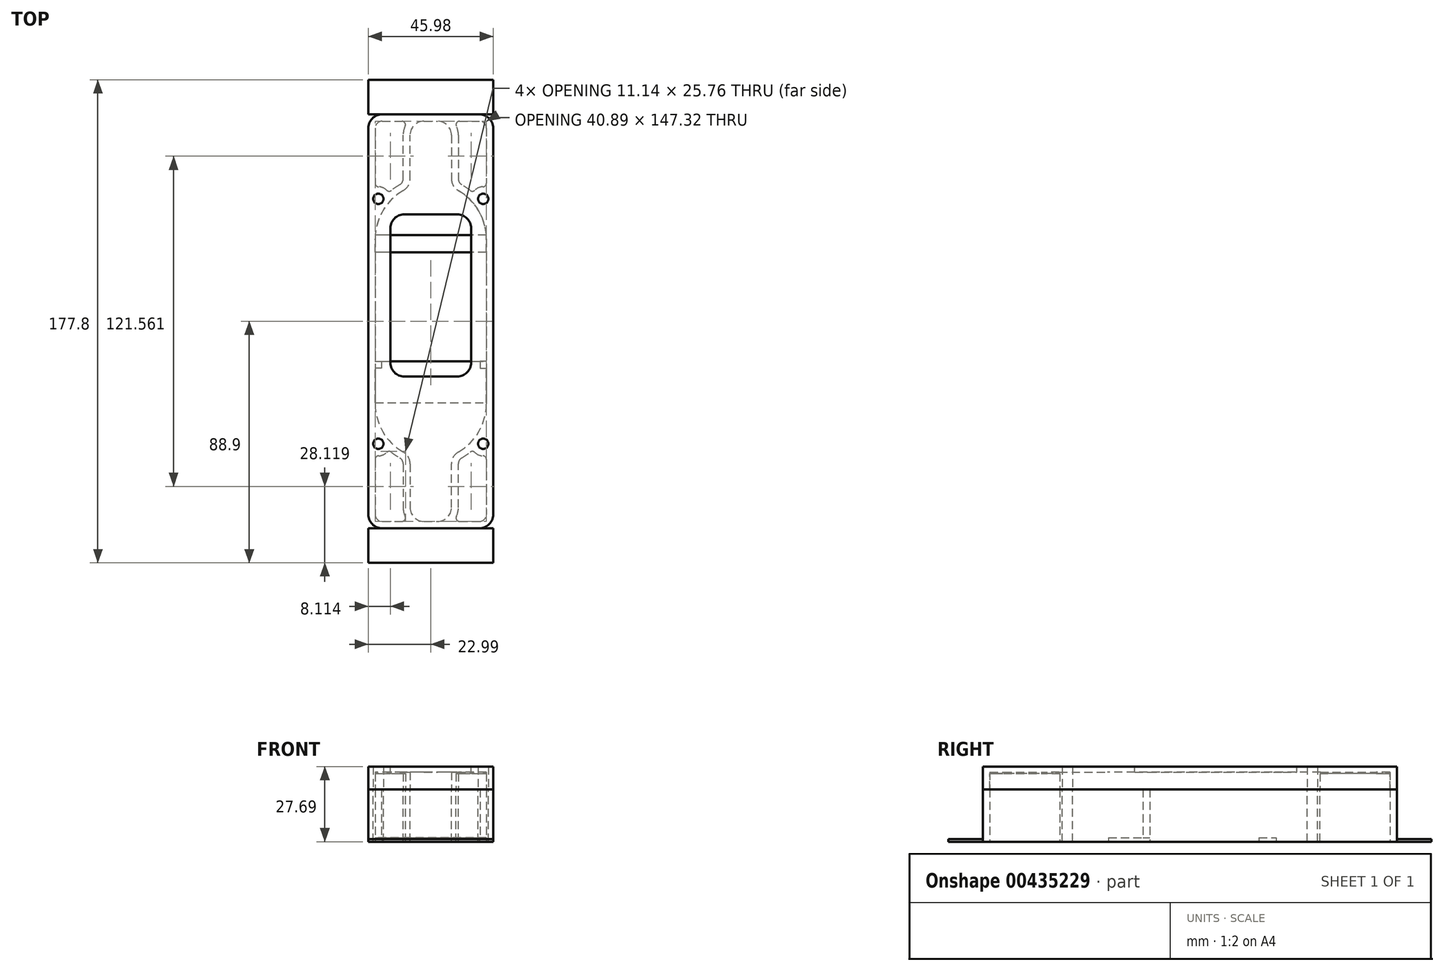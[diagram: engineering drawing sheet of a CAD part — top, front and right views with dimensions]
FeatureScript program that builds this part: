
annotation { "Feature Type Name" : "Feature", "Feature Type Description" : "" }
export const myFeature = defineFeature(function(context is Context, id is Id, definition is map)
    precondition{}
    {
        {
            var Q0;
            Q0=qCreatedBy(makeId("Top.planeOp"),FACE);
            var sketch = newSketch(context, id + "F0", { "sketchPlane" : qUnion([Q0])});
            skArc(sketch, "E0", {"start": v(20.45, 30.35) * mm, "mid": v(16.94, 41.8) * mm, "end": v(7.62, 49.33) * mm});
            skArc(sketch, "E1", {"start": v(-20.45, -30.35) * mm, "mid": v(-16.94, -41.8) * mm, "end": v(-7.62, -49.33) * mm});
            skLineSegment(sketch, "E2", {"start": v(20.45, 30.35) * mm, "end": v(20.45, -14.73) * mm});
            skLineSegment(sketch, "E3", {"start": v(-20.45, 30.35) * mm, "end": v(-20.45, -14.73) * mm});
            skPoint(sketch, "E4", {"position": v(0, 50.8) * mm});
            skPoint(sketch, "E5", {"position": v(0, -50.8) * mm});
            skPoint(sketch, "E6", {"position": v(-20.45, 0) * mm});
            skLineSegment(sketch, "E7", {"start": v(-20.45, -14.73) * mm, "end": v(-18.16, -14.73) * mm});
            skLineSegment(sketch, "E8", {"start": v(-18.16, -14.73) * mm, "end": v(-18.16, -17.27) * mm});
            skLineSegment(sketch, "E9", {"start": v(-18.16, -17.27) * mm, "end": v(-20.45, -17.27) * mm});
            skLineSegment(sketch, "E10", {"start": v(20.45, -14.73) * mm, "end": v(18.16, -14.73) * mm});
            skLineSegment(sketch, "E11", {"start": v(18.16, -14.73) * mm, "end": v(18.16, -17.27) * mm});
            skLineSegment(sketch, "E12", {"start": v(18.16, -17.27) * mm, "end": v(20.45, -17.27) * mm});
            skLineSegment(sketch, "E13", {"start": v(-20.45, -14.73) * mm, "end": v(-20.45, -17.27) * mm, "construction": true});
            skLineSegment(sketch, "E14", {"start": v(-20.45, -17.27) * mm, "end": v(-20.45, -30.35) * mm});
            skLineSegment(sketch, "E15", {"start": v(20.45, -17.27) * mm, "end": v(20.45, -30.35) * mm});
            skLineSegment(sketch, "E16", {"start": v(20.45, -14.73) * mm, "end": v(20.45, -17.27) * mm, "construction": true});
            skLineSegment(sketch, "E17", {"start": v(-18.16, -14.73) * mm, "end": v(18.16, -14.73) * mm, "construction": true});
            skPoint(sketch, "E18", {"position": v(0, -14.73) * mm});
            skLineSegment(sketch, "E19.bottom", {"start": v(-22.99, 76.2) * mm, "end": v(22.99, 76.2) * mm});
            skLineSegment(sketch, "E19.top", {"start": v(-22.99, -76.2) * mm, "end": v(22.99, -76.2) * mm});
            skLineSegment(sketch, "E19.left", {"start": v(-22.99, 76.2) * mm, "end": v(-22.99, -76.2) * mm});
            skLineSegment(sketch, "E19.right", {"start": v(22.99, 76.2) * mm, "end": v(22.99, -76.2) * mm});
            skPoint(sketch, "E20", {"position": v(0, 76.2) * mm});
            skPoint(sketch, "E21", {"position": v(-22.99, 0) * mm});
            skLineSegment(sketch, "E22", {"start": v(-7.62, 49.33) * mm, "end": v(-7.62, 73.66) * mm});
            skLineSegment(sketch, "E23", {"start": v(-7.62, 73.66) * mm, "end": v(7.62, 73.66) * mm});
            skLineSegment(sketch, "E24", {"start": v(7.62, 73.66) * mm, "end": v(7.62, 49.33) * mm});
            skArc(sketch, "E25", {"start": v(-7.62, 49.33) * mm, "mid": v(-16.94, 41.8) * mm, "end": v(-20.45, 30.35) * mm});
            skArc(sketch, "E26", {"start": v(7.62, 49.33) * mm, "mid": v(0, 50.8) * mm, "end": v(-7.62, 49.33) * mm, "construction": true});
            skLineSegment(sketch, "E27", {"start": v(-20.45, 30.35) * mm, "end": v(-22.99, 30.35) * mm, "construction": true});
            skLineSegment(sketch, "E28", {"start": v(-7.62, 73.66) * mm, "end": v(-7.62, 76.2) * mm, "construction": true});
            skLineSegment(sketch, "E29", {"start": v(-7.62, -49.33) * mm, "end": v(-7.62, -73.66) * mm});
            skLineSegment(sketch, "E30", {"start": v(-7.62, -73.66) * mm, "end": v(7.62, -73.66) * mm});
            skLineSegment(sketch, "E31", {"start": v(7.62, -73.66) * mm, "end": v(7.62, -49.33) * mm});
            skArc(sketch, "E32", {"start": v(7.62, -49.33) * mm, "mid": v(16.94, -41.8) * mm, "end": v(20.45, -30.35) * mm});
            skArc(sketch, "E33", {"start": v(-7.62, -49.33) * mm, "mid": v(0, -50.8) * mm, "end": v(7.62, -49.33) * mm, "construction": true});
            skSolve(sketch);
        }
        {
            var Q0;
            Q0 = qSketchRegion(id + "F0", true);
            extrude(context, id + "F1", {"entities" : qUnion([Q0]), "depth" : 19.3 * mm});
        }
        {
            var Q0;
            Q0=makeQuery(id+"F1.opExtrude","CAP_FACE",FACE,{"disambiguationData":[OSD([sQuery(id+"F0.wireOp",EDGE,"E0"),sQuery(id+"F0.wireOp",EDGE,"E1"),sQuery(id+"F0.wireOp",EDGE,"E2"),sQuery(id+"F0.wireOp",EDGE,"E3"),sQuery(id+"F0.wireOp",EDGE,"E7"),sQuery(id+"F0.wireOp",EDGE,"E8"),sQuery(id+"F0.wireOp",EDGE,"E9"),sQuery(id+"F0.wireOp",EDGE,"E10"),sQuery(id+"F0.wireOp",EDGE,"E11"),sQuery(id+"F0.wireOp",EDGE,"E12"),sQuery(id+"F0.wireOp",EDGE,"E14"),sQuery(id+"F0.wireOp",EDGE,"E15"),sQuery(id+"F0.wireOp",EDGE,"E19.bottom"),sQuery(id+"F0.wireOp",EDGE,"E19.top"),sQuery(id+"F0.wireOp",EDGE,"E19.left"),sQuery(id+"F0.wireOp",EDGE,"E19.right"),sQuery(id+"F0.wireOp",EDGE,"E22"),sQuery(id+"F0.wireOp",EDGE,"E23"),sQuery(id+"F0.wireOp",EDGE,"E24"),sQuery(id+"F0.wireOp",EDGE,"E25"),sQuery(id+"F0.wireOp",EDGE,"E29"),sQuery(id+"F0.wireOp",EDGE,"E30"),sQuery(id+"F0.wireOp",EDGE,"E31"),sQuery(id+"F0.wireOp",EDGE,"E32")])],"isStart":true});
            var sketch = newSketch(context, id + "F2", { "sketchPlane" : qUnion([Q0])});
            skLineSegment(sketch, "E34.bottom", {"start": v(-20.45, 29.97) * mm, "end": v(20.45, 29.97) * mm});
            skLineSegment(sketch, "E34.top", {"start": v(-20.45, 14.73) * mm, "end": v(20.45, 14.73) * mm});
            skLineSegment(sketch, "E34.left", {"start": v(-20.45, 29.97) * mm, "end": v(-20.45, 14.73) * mm});
            skLineSegment(sketch, "E34.right", {"start": v(20.45, 29.97) * mm, "end": v(20.45, 14.73) * mm});
            skLineSegment(sketch, "E35.bottom", {"start": v(20.45, -25.4) * mm, "end": v(-20.45, -25.4) * mm});
            skLineSegment(sketch, "E35.top", {"start": v(20.45, -31.75) * mm, "end": v(-20.45, -31.75) * mm});
            skLineSegment(sketch, "E35.left", {"start": v(20.45, -25.4) * mm, "end": v(20.45, -31.75) * mm});
            skLineSegment(sketch, "E35.right", {"start": v(-20.45, -25.4) * mm, "end": v(-20.45, -31.75) * mm});
            skPoint(sketch, "E36", {"position": v(-20.45, 22.35) * mm});
            skSolve(sketch);
        }
        {
            var Q0;
            Q0 = qSketchRegion(id + "F2", true);
            extrude(context, id + "F3", {"entities" : qUnion([Q0]), "operationType" : NewBodyOperationType.ADD, "oppositeDirection" : true, "depth" : 1.52 * mm});
        }
        {
            var Q0;
            Q0=makeQuery(id+"FgRfp3muFPT9lto_1.boolean.opBoolean","MERGE",EDGE,{"derivedFrom":[makeQuery(id+"F1.opExtrude","SWEPT_EDGE",EDGE,{"disambiguationData":[OSD([sQuery(id+"F0.wireOp",EDGE,"E19.bottom"),sQuery(id+"F0.wireOp",EDGE,"E19.left")])]}),makeQuery(id+"FgRfp3muFPT9lto_1.opExtrude","SWEPT_EDGE",EDGE,{"disambiguationData":[OSD([sQuery(id+"Ftx3Hq8NVKijBld_1.wireOp",EDGE,"g6n0YkWi-r8fi-JQox-6JIj-wQ41cYzrdf4m.top"),sQuery(id+"Ftx3Hq8NVKijBld_1.wireOp",EDGE,"g6n0YkWi-r8fi-JQox-6JIj-wQ41cYzrdf4m.right")])]})]});
            var Q1;
            Q1=makeQuery(id+"FgRfp3muFPT9lto_1.boolean.opBoolean","MERGE",EDGE,{"derivedFrom":[makeQuery(id+"F1.opExtrude","SWEPT_EDGE",EDGE,{"disambiguationData":[OSD([sQuery(id+"F0.wireOp",EDGE,"E19.top"),sQuery(id+"F0.wireOp",EDGE,"E19.left")])]}),makeQuery(id+"FgRfp3muFPT9lto_1.opExtrude","SWEPT_EDGE",EDGE,{"disambiguationData":[OSD([sQuery(id+"Ftx3Hq8NVKijBld_1.wireOp",EDGE,"g6n0YkWi-r8fi-JQox-6JIj-wQ41cYzrdf4m.bottom"),sQuery(id+"Ftx3Hq8NVKijBld_1.wireOp",EDGE,"g6n0YkWi-r8fi-JQox-6JIj-wQ41cYzrdf4m.right")])]})]});
            var Q2;
            Q2=makeQuery(id+"FgRfp3muFPT9lto_1.boolean.opBoolean","MERGE",EDGE,{"derivedFrom":[makeQuery(id+"F1.opExtrude","SWEPT_EDGE",EDGE,{"disambiguationData":[OSD([sQuery(id+"F0.wireOp",EDGE,"E19.top"),sQuery(id+"F0.wireOp",EDGE,"E19.right")])]}),makeQuery(id+"FgRfp3muFPT9lto_1.opExtrude","SWEPT_EDGE",EDGE,{"disambiguationData":[OSD([sQuery(id+"Ftx3Hq8NVKijBld_1.wireOp",EDGE,"g6n0YkWi-r8fi-JQox-6JIj-wQ41cYzrdf4m.bottom"),sQuery(id+"Ftx3Hq8NVKijBld_1.wireOp",EDGE,"g6n0YkWi-r8fi-JQox-6JIj-wQ41cYzrdf4m.left")])]})]});
            var Q3;
            Q3=makeQuery(id+"FgRfp3muFPT9lto_1.boolean.opBoolean","MERGE",EDGE,{"derivedFrom":[makeQuery(id+"F1.opExtrude","SWEPT_EDGE",EDGE,{"disambiguationData":[OSD([sQuery(id+"F0.wireOp",EDGE,"E19.bottom"),sQuery(id+"F0.wireOp",EDGE,"E19.right")])]}),makeQuery(id+"FgRfp3muFPT9lto_1.opExtrude","SWEPT_EDGE",EDGE,{"disambiguationData":[OSD([sQuery(id+"Ftx3Hq8NVKijBld_1.wireOp",EDGE,"g6n0YkWi-r8fi-JQox-6JIj-wQ41cYzrdf4m.top"),sQuery(id+"Ftx3Hq8NVKijBld_1.wireOp",EDGE,"g6n0YkWi-r8fi-JQox-6JIj-wQ41cYzrdf4m.left")])]})]});
            var Q4;
            Q4=makeQuery(id+"FgRfp3muFPT9lto_1.boolean.opBoolean","MERGE",EDGE,{"derivedFrom":[makeQuery(id+"F1.opExtrude","SWEPT_EDGE",EDGE,{"disambiguationData":[OSD([sQuery(id+"F0.wireOp",EDGE,"E23"),sQuery(id+"F0.wireOp",EDGE,"E24")])]}),makeQuery(id+"FgRfp3muFPT9lto_1.opExtrude","SWEPT_EDGE",EDGE,{"disambiguationData":[OSD([sQuery(id+"Ftx3Hq8NVKijBld_1.wireOp",EDGE,"3AGzFTSj-HEBm-45NR-ugF2-llzYKDWyuuH7.bottom"),sQuery(id+"Ftx3Hq8NVKijBld_1.wireOp",EDGE,"3AGzFTSj-HEBm-45NR-ugF2-llzYKDWyuuH7.left")])]})]});
            var Q5;
            Q5=makeQuery(id+"FgRfp3muFPT9lto_1.boolean.opBoolean","MERGE",EDGE,{"derivedFrom":[makeQuery(id+"F1.opExtrude","SWEPT_EDGE",EDGE,{"disambiguationData":[OSD([sQuery(id+"F0.wireOp",EDGE,"E22"),sQuery(id+"F0.wireOp",EDGE,"E23")])]}),makeQuery(id+"FgRfp3muFPT9lto_1.opExtrude","SWEPT_EDGE",EDGE,{"disambiguationData":[OSD([sQuery(id+"Ftx3Hq8NVKijBld_1.wireOp",EDGE,"3AGzFTSj-HEBm-45NR-ugF2-llzYKDWyuuH7.bottom"),sQuery(id+"Ftx3Hq8NVKijBld_1.wireOp",EDGE,"3AGzFTSj-HEBm-45NR-ugF2-llzYKDWyuuH7.right")])]})]});
            var Q6;
            Q6=makeQuery(id+"F1.opExtrude","SWEPT_EDGE",EDGE,{"disambiguationData":[OSD([sQuery(id+"F0.wireOp",EDGE,"E22"),sQuery(id+"F0.wireOp",EDGE,"E25")])]});
            var Q7;
            Q7=makeQuery(id+"F1.opExtrude","SWEPT_EDGE",EDGE,{"disambiguationData":[OSD([sQuery(id+"F0.wireOp",EDGE,"E0"),sQuery(id+"F0.wireOp",EDGE,"E24")])]});
            var Q8;
            Q8=makeQuery(id+"F1.opExtrude","SWEPT_EDGE",EDGE,{"disambiguationData":[OSD([sQuery(id+"F0.wireOp",EDGE,"E1"),sQuery(id+"F0.wireOp",EDGE,"E29")])]});
            var Q9;
            Q9=makeQuery(id+"FgRfp3muFPT9lto_1.boolean.opBoolean","MERGE",EDGE,{"derivedFrom":[makeQuery(id+"F1.opExtrude","SWEPT_EDGE",EDGE,{"disambiguationData":[OSD([sQuery(id+"F0.wireOp",EDGE,"E29"),sQuery(id+"F0.wireOp",EDGE,"E30")])]}),makeQuery(id+"FgRfp3muFPT9lto_1.opExtrude","SWEPT_EDGE",EDGE,{"disambiguationData":[OSD([sQuery(id+"Ftx3Hq8NVKijBld_1.wireOp",EDGE,"SY61azI3-jvyg-wfIl-SQMA-vttAN6HS4ba1.bottom"),sQuery(id+"Ftx3Hq8NVKijBld_1.wireOp",EDGE,"SY61azI3-jvyg-wfIl-SQMA-vttAN6HS4ba1.right")])]})]});
            var Q10;
            Q10=makeQuery(id+"FgRfp3muFPT9lto_1.boolean.opBoolean","MERGE",EDGE,{"derivedFrom":[makeQuery(id+"F1.opExtrude","SWEPT_EDGE",EDGE,{"disambiguationData":[OSD([sQuery(id+"F0.wireOp",EDGE,"E30"),sQuery(id+"F0.wireOp",EDGE,"E31")])]}),makeQuery(id+"FgRfp3muFPT9lto_1.opExtrude","SWEPT_EDGE",EDGE,{"disambiguationData":[OSD([sQuery(id+"Ftx3Hq8NVKijBld_1.wireOp",EDGE,"SY61azI3-jvyg-wfIl-SQMA-vttAN6HS4ba1.bottom"),sQuery(id+"Ftx3Hq8NVKijBld_1.wireOp",EDGE,"SY61azI3-jvyg-wfIl-SQMA-vttAN6HS4ba1.left")])]})]});
            var Q11;
            Q11=makeQuery(id+"F1.opExtrude","SWEPT_EDGE",EDGE,{"disambiguationData":[OSD([sQuery(id+"F0.wireOp",EDGE,"E31"),sQuery(id+"F0.wireOp",EDGE,"E32")])]});
            var Q12;
            Q12=makeQuery(id+"FgRfp3muFPT9lto_1.opExtrude","SWEPT_EDGE",EDGE,{"disambiguationData":[OSD([sQuery(id+"Ftx3Hq8NVKijBld_1.wireOp",EDGE,"3AGzFTSj-HEBm-45NR-ugF2-llzYKDWyuuH7.top"),sQuery(id+"Ftx3Hq8NVKijBld_1.wireOp",EDGE,"3AGzFTSj-HEBm-45NR-ugF2-llzYKDWyuuH7.right")])]});
            var Q13;
            Q13=makeQuery(id+"FgRfp3muFPT9lto_1.opExtrude","SWEPT_EDGE",EDGE,{"disambiguationData":[OSD([sQuery(id+"Ftx3Hq8NVKijBld_1.wireOp",EDGE,"3AGzFTSj-HEBm-45NR-ugF2-llzYKDWyuuH7.top"),sQuery(id+"Ftx3Hq8NVKijBld_1.wireOp",EDGE,"3AGzFTSj-HEBm-45NR-ugF2-llzYKDWyuuH7.left")])]});
            var Q14;
            Q14=makeQuery(id+"FgRfp3muFPT9lto_1.opExtrude","SWEPT_EDGE",EDGE,{"disambiguationData":[OSD([sQuery(id+"Ftx3Hq8NVKijBld_1.wireOp",EDGE,"f7xWbKYU-4XlC-xXvP-zV3z-Gg6iEQBUtCaq.bottom"),sQuery(id+"Ftx3Hq8NVKijBld_1.wireOp",EDGE,"f7xWbKYU-4XlC-xXvP-zV3z-Gg6iEQBUtCaq.right")])]});
            var Q15;
            Q15=makeQuery(id+"FgRfp3muFPT9lto_1.opExtrude","SWEPT_EDGE",EDGE,{"disambiguationData":[OSD([sQuery(id+"Ftx3Hq8NVKijBld_1.wireOp",EDGE,"f7xWbKYU-4XlC-xXvP-zV3z-Gg6iEQBUtCaq.bottom"),sQuery(id+"Ftx3Hq8NVKijBld_1.wireOp",EDGE,"f7xWbKYU-4XlC-xXvP-zV3z-Gg6iEQBUtCaq.left")])]});
            var Q16;
            Q16=makeQuery(id+"FgRfp3muFPT9lto_1.opExtrude","SWEPT_EDGE",EDGE,{"disambiguationData":[OSD([sQuery(id+"Ftx3Hq8NVKijBld_1.wireOp",EDGE,"SY61azI3-jvyg-wfIl-SQMA-vttAN6HS4ba1.top"),sQuery(id+"Ftx3Hq8NVKijBld_1.wireOp",EDGE,"SY61azI3-jvyg-wfIl-SQMA-vttAN6HS4ba1.right")])]});
            var Q17;
            Q17=makeQuery(id+"FgRfp3muFPT9lto_1.opExtrude","SWEPT_EDGE",EDGE,{"disambiguationData":[OSD([sQuery(id+"Ftx3Hq8NVKijBld_1.wireOp",EDGE,"SY61azI3-jvyg-wfIl-SQMA-vttAN6HS4ba1.top"),sQuery(id+"Ftx3Hq8NVKijBld_1.wireOp",EDGE,"SY61azI3-jvyg-wfIl-SQMA-vttAN6HS4ba1.left")])]});
            var Q18;
            Q18=makeQuery(id+"FgRfp3muFPT9lto_1.opExtrude","SWEPT_EDGE",EDGE,{"disambiguationData":[OSD([sQuery(id+"Ftx3Hq8NVKijBld_1.wireOp",EDGE,"f7xWbKYU-4XlC-xXvP-zV3z-Gg6iEQBUtCaq.top"),sQuery(id+"Ftx3Hq8NVKijBld_1.wireOp",EDGE,"f7xWbKYU-4XlC-xXvP-zV3z-Gg6iEQBUtCaq.right")])]});
            var Q19;
            Q19=makeQuery(id+"FgRfp3muFPT9lto_1.opExtrude","SWEPT_EDGE",EDGE,{"disambiguationData":[OSD([sQuery(id+"Ftx3Hq8NVKijBld_1.wireOp",EDGE,"f7xWbKYU-4XlC-xXvP-zV3z-Gg6iEQBUtCaq.top"),sQuery(id+"Ftx3Hq8NVKijBld_1.wireOp",EDGE,"f7xWbKYU-4XlC-xXvP-zV3z-Gg6iEQBUtCaq.left")])]});
            fillet(context, id + "F4", {"entities" : qUnion([Q0, Q1, Q2, Q3, Q4, Q5, Q6, Q7, Q8, Q9, Q10, Q11, Q12, Q13, Q14, Q15, Q16, Q17, Q18, Q19]), "radius" : 5.08 * mm, "tangentPropagation" : true, "allowEdgeOverflow" : false});
        }
        {
            var Q0;
            Q0=makeQuery(id+"F1.opExtrude","CAP_FACE",FACE,{"disambiguationData":[OSD([sQuery(id+"F0.wireOp",EDGE,"E0"),sQuery(id+"F0.wireOp",EDGE,"E1"),sQuery(id+"F0.wireOp",EDGE,"E2"),sQuery(id+"F0.wireOp",EDGE,"E3"),sQuery(id+"F0.wireOp",EDGE,"E7"),sQuery(id+"F0.wireOp",EDGE,"E8"),sQuery(id+"F0.wireOp",EDGE,"E9"),sQuery(id+"F0.wireOp",EDGE,"E10"),sQuery(id+"F0.wireOp",EDGE,"E11"),sQuery(id+"F0.wireOp",EDGE,"E12"),sQuery(id+"F0.wireOp",EDGE,"E14"),sQuery(id+"F0.wireOp",EDGE,"E15"),sQuery(id+"F0.wireOp",EDGE,"E19.bottom"),sQuery(id+"F0.wireOp",EDGE,"E19.top"),sQuery(id+"F0.wireOp",EDGE,"E19.left"),sQuery(id+"F0.wireOp",EDGE,"E19.right"),sQuery(id+"F0.wireOp",EDGE,"E22"),sQuery(id+"F0.wireOp",EDGE,"E23"),sQuery(id+"F0.wireOp",EDGE,"E24"),sQuery(id+"F0.wireOp",EDGE,"E25"),sQuery(id+"F0.wireOp",EDGE,"E29"),sQuery(id+"F0.wireOp",EDGE,"E30"),sQuery(id+"F0.wireOp",EDGE,"E31"),sQuery(id+"F0.wireOp",EDGE,"E32")])],"isStart":false});
            var sketch = newSketch(context, id + "F5", { "sketchPlane" : qUnion([Q0])});
            skCircle(sketch, "E37", {"center": v(-19.3, 45.09) * mm, "radius": 1.9 * mm});
            skLineSegment(sketch, "E38.bottom", {"start": v(-19.3, 45.09) * mm, "end": v(19.3, 45.09) * mm, "construction": true});
            skLineSegment(sketch, "E38.top", {"start": v(-19.3, -45.09) * mm, "end": v(19.3, -45.09) * mm, "construction": true});
            skLineSegment(sketch, "E38.left", {"start": v(-19.3, 45.09) * mm, "end": v(-19.3, -45.09) * mm, "construction": true});
            skLineSegment(sketch, "E38.right", {"start": v(19.3, 45.09) * mm, "end": v(19.3, -45.09) * mm, "construction": true});
            skPoint(sketch, "E39", {"position": v(-19.3, 0) * mm});
            skPoint(sketch, "E40", {"position": v(0, 45.09) * mm});
            skCircle(sketch, "E41", {"center": v(19.3, 45.09) * mm, "radius": 1.9 * mm});
            skCircle(sketch, "E42", {"center": v(19.3, -45.09) * mm, "radius": 1.9 * mm});
            skCircle(sketch, "E43", {"center": v(-19.3, -45.09) * mm, "radius": 1.9 * mm});
            skSolve(sketch);
        }
        {
            var Q0;
            Q0 = qSketchRegion(id + "F5", true);
            var Q1;
            Q1=makeQuery(id+"F3.boolean.opBoolean","MERGE",FACE,{"derivedFrom":[makeQuery(id+"F1.opExtrude","CAP_FACE",FACE,{"disambiguationData":[OSD([sQuery(id+"F0.wireOp",EDGE,"E0"),sQuery(id+"F0.wireOp",EDGE,"E1"),sQuery(id+"F0.wireOp",EDGE,"E2"),sQuery(id+"F0.wireOp",EDGE,"E3"),sQuery(id+"F0.wireOp",EDGE,"E7"),sQuery(id+"F0.wireOp",EDGE,"E8"),sQuery(id+"F0.wireOp",EDGE,"E9"),sQuery(id+"F0.wireOp",EDGE,"E10"),sQuery(id+"F0.wireOp",EDGE,"E11"),sQuery(id+"F0.wireOp",EDGE,"E12"),sQuery(id+"F0.wireOp",EDGE,"E14"),sQuery(id+"F0.wireOp",EDGE,"E15"),sQuery(id+"F0.wireOp",EDGE,"E19.bottom"),sQuery(id+"F0.wireOp",EDGE,"E19.top"),sQuery(id+"F0.wireOp",EDGE,"E19.left"),sQuery(id+"F0.wireOp",EDGE,"E19.right"),sQuery(id+"F0.wireOp",EDGE,"E22"),sQuery(id+"F0.wireOp",EDGE,"E23"),sQuery(id+"F0.wireOp",EDGE,"E24"),sQuery(id+"F0.wireOp",EDGE,"E25"),sQuery(id+"F0.wireOp",EDGE,"E29"),sQuery(id+"F0.wireOp",EDGE,"E30"),sQuery(id+"F0.wireOp",EDGE,"E31"),sQuery(id+"F0.wireOp",EDGE,"E32")])],"isStart":true}),makeQuery(id+"F3.opExtrude","CAP_FACE",FACE,{"disambiguationData":[OSD([sQuery(id+"F2.wireOp",EDGE,"E34.bottom"),sQuery(id+"F2.wireOp",EDGE,"E34.top"),sQuery(id+"F2.wireOp",EDGE,"E34.left"),sQuery(id+"F2.wireOp",EDGE,"E34.right")])],"isStart":true}),makeQuery(id+"F3.opExtrude","CAP_FACE",FACE,{"disambiguationData":[OSD([sQuery(id+"F2.wireOp",EDGE,"E35.bottom"),sQuery(id+"F2.wireOp",EDGE,"E35.top"),sQuery(id+"F2.wireOp",EDGE,"E35.left"),sQuery(id+"F2.wireOp",EDGE,"E35.right")])],"isStart":true})]});
            extrude(context, id + "F6", {"entities" : qUnion([Q0]), "operationType" : NewBodyOperationType.REMOVE, "endBound" : BoundingType.UP_TO_SURFACE, "oppositeDirection" : true, "endBoundEntityFace" : qUnion([Q1]), "depth" : 25.4 * mm});
        }
        {
            var Q0;
            Q0=makeQuery(id+"F1.opExtrude","CAP_FACE",FACE,{"disambiguationData":[OSD([sQuery(id+"F0.wireOp",EDGE,"E0"),sQuery(id+"F0.wireOp",EDGE,"E1"),sQuery(id+"F0.wireOp",EDGE,"E2"),sQuery(id+"F0.wireOp",EDGE,"E3"),sQuery(id+"F0.wireOp",EDGE,"E7"),sQuery(id+"F0.wireOp",EDGE,"E8"),sQuery(id+"F0.wireOp",EDGE,"E9"),sQuery(id+"F0.wireOp",EDGE,"E10"),sQuery(id+"F0.wireOp",EDGE,"E11"),sQuery(id+"F0.wireOp",EDGE,"E12"),sQuery(id+"F0.wireOp",EDGE,"E14"),sQuery(id+"F0.wireOp",EDGE,"E15"),sQuery(id+"F0.wireOp",EDGE,"E19.bottom"),sQuery(id+"F0.wireOp",EDGE,"E19.top"),sQuery(id+"F0.wireOp",EDGE,"E19.left"),sQuery(id+"F0.wireOp",EDGE,"E19.right"),sQuery(id+"F0.wireOp",EDGE,"E22"),sQuery(id+"F0.wireOp",EDGE,"E23"),sQuery(id+"F0.wireOp",EDGE,"E24"),sQuery(id+"F0.wireOp",EDGE,"E25"),sQuery(id+"F0.wireOp",EDGE,"E29"),sQuery(id+"F0.wireOp",EDGE,"E30"),sQuery(id+"F0.wireOp",EDGE,"E31"),sQuery(id+"F0.wireOp",EDGE,"E32")])],"isStart":false});
            var Q1;
            Q1=makeQuery(id+"F1.opExtrude","SWEPT_BODY",BODY,{"disambiguationData":[OSD([sQuery(id+"F0.wireOp",EDGE,"E0"),sQuery(id+"F0.wireOp",EDGE,"E1"),sQuery(id+"F0.wireOp",EDGE,"E2"),sQuery(id+"F0.wireOp",EDGE,"E3"),sQuery(id+"F0.wireOp",EDGE,"E7"),sQuery(id+"F0.wireOp",EDGE,"E8"),sQuery(id+"F0.wireOp",EDGE,"E9"),sQuery(id+"F0.wireOp",EDGE,"E10"),sQuery(id+"F0.wireOp",EDGE,"E11"),sQuery(id+"F0.wireOp",EDGE,"E12"),sQuery(id+"F0.wireOp",EDGE,"E14"),sQuery(id+"F0.wireOp",EDGE,"E15"),sQuery(id+"F0.wireOp",EDGE,"E19.bottom"),sQuery(id+"F0.wireOp",EDGE,"E19.top"),sQuery(id+"F0.wireOp",EDGE,"E19.left"),sQuery(id+"F0.wireOp",EDGE,"E19.right"),sQuery(id+"F0.wireOp",EDGE,"E22"),sQuery(id+"F0.wireOp",EDGE,"E23"),sQuery(id+"F0.wireOp",EDGE,"E24"),sQuery(id+"F0.wireOp",EDGE,"E25"),sQuery(id+"F0.wireOp",EDGE,"E29"),sQuery(id+"F0.wireOp",EDGE,"E30"),sQuery(id+"F0.wireOp",EDGE,"E31"),sQuery(id+"F0.wireOp",EDGE,"E32")])]});
            shell(context, id + "F7", {"entities" : qUnion([Q0]), "parts" : qUnion([Q1]), "thickness" : 2.54 * mm});
        }
        {
            var Q0;
            Q0=makeQuery(id+"F7.opShell","OFFSET_FACE",FACE,{"disambiguationData":[OSD([sQuery(id+"F0.wireOp",EDGE,"E0"),sQuery(id+"F0.wireOp",EDGE,"E1"),sQuery(id+"F0.wireOp",EDGE,"E2"),sQuery(id+"F0.wireOp",EDGE,"E3"),sQuery(id+"F0.wireOp",EDGE,"E7"),sQuery(id+"F0.wireOp",EDGE,"E8"),sQuery(id+"F0.wireOp",EDGE,"E9"),sQuery(id+"F0.wireOp",EDGE,"E10"),sQuery(id+"F0.wireOp",EDGE,"E11"),sQuery(id+"F0.wireOp",EDGE,"E12"),sQuery(id+"F0.wireOp",EDGE,"E14"),sQuery(id+"F0.wireOp",EDGE,"E15"),sQuery(id+"F0.wireOp",EDGE,"E19.bottom"),sQuery(id+"F0.wireOp",EDGE,"E19.top"),sQuery(id+"F0.wireOp",EDGE,"E19.left"),sQuery(id+"F0.wireOp",EDGE,"E19.right"),sQuery(id+"F0.wireOp",EDGE,"E22"),sQuery(id+"F0.wireOp",EDGE,"E23"),sQuery(id+"F0.wireOp",EDGE,"E24"),sQuery(id+"F0.wireOp",EDGE,"E25"),sQuery(id+"F0.wireOp",EDGE,"E29"),sQuery(id+"F0.wireOp",EDGE,"E30"),sQuery(id+"F0.wireOp",EDGE,"E31"),sQuery(id+"F0.wireOp",EDGE,"E32"),sQuery(id+"F2.wireOp",EDGE,"E34.bottom"),sQuery(id+"F2.wireOp",EDGE,"E34.top"),sQuery(id+"F2.wireOp",EDGE,"E34.left"),sQuery(id+"F2.wireOp",EDGE,"E34.right"),sQuery(id+"F2.wireOp",EDGE,"E35.bottom"),sQuery(id+"F2.wireOp",EDGE,"E35.top"),sQuery(id+"F2.wireOp",EDGE,"E35.left"),sQuery(id+"F2.wireOp",EDGE,"E35.right")]),OD(2.0)]});
            var Q1;
            Q1=makeQuery(id+"F7.opShell","OFFSET_FACE",FACE,{"disambiguationData":[OSD([sQuery(id+"F0.wireOp",EDGE,"E0"),sQuery(id+"F0.wireOp",EDGE,"E1"),sQuery(id+"F0.wireOp",EDGE,"E2"),sQuery(id+"F0.wireOp",EDGE,"E3"),sQuery(id+"F0.wireOp",EDGE,"E7"),sQuery(id+"F0.wireOp",EDGE,"E8"),sQuery(id+"F0.wireOp",EDGE,"E9"),sQuery(id+"F0.wireOp",EDGE,"E10"),sQuery(id+"F0.wireOp",EDGE,"E11"),sQuery(id+"F0.wireOp",EDGE,"E12"),sQuery(id+"F0.wireOp",EDGE,"E14"),sQuery(id+"F0.wireOp",EDGE,"E15"),sQuery(id+"F0.wireOp",EDGE,"E19.bottom"),sQuery(id+"F0.wireOp",EDGE,"E19.top"),sQuery(id+"F0.wireOp",EDGE,"E19.left"),sQuery(id+"F0.wireOp",EDGE,"E19.right"),sQuery(id+"F0.wireOp",EDGE,"E22"),sQuery(id+"F0.wireOp",EDGE,"E23"),sQuery(id+"F0.wireOp",EDGE,"E24"),sQuery(id+"F0.wireOp",EDGE,"E25"),sQuery(id+"F0.wireOp",EDGE,"E29"),sQuery(id+"F0.wireOp",EDGE,"E30"),sQuery(id+"F0.wireOp",EDGE,"E31"),sQuery(id+"F0.wireOp",EDGE,"E32"),sQuery(id+"F2.wireOp",EDGE,"E34.bottom"),sQuery(id+"F2.wireOp",EDGE,"E34.top"),sQuery(id+"F2.wireOp",EDGE,"E34.left"),sQuery(id+"F2.wireOp",EDGE,"E34.right"),sQuery(id+"F2.wireOp",EDGE,"E35.bottom"),sQuery(id+"F2.wireOp",EDGE,"E35.top"),sQuery(id+"F2.wireOp",EDGE,"E35.left"),sQuery(id+"F2.wireOp",EDGE,"E35.right")]),OD(0.0)]});
            var Q2;
            Q2=makeQuery(id+"F7.opShell","OFFSET_FACE",FACE,{"disambiguationData":[OSD([sQuery(id+"F0.wireOp",EDGE,"E0"),sQuery(id+"F0.wireOp",EDGE,"E1"),sQuery(id+"F0.wireOp",EDGE,"E2"),sQuery(id+"F0.wireOp",EDGE,"E3"),sQuery(id+"F0.wireOp",EDGE,"E7"),sQuery(id+"F0.wireOp",EDGE,"E8"),sQuery(id+"F0.wireOp",EDGE,"E9"),sQuery(id+"F0.wireOp",EDGE,"E10"),sQuery(id+"F0.wireOp",EDGE,"E11"),sQuery(id+"F0.wireOp",EDGE,"E12"),sQuery(id+"F0.wireOp",EDGE,"E14"),sQuery(id+"F0.wireOp",EDGE,"E15"),sQuery(id+"F0.wireOp",EDGE,"E19.bottom"),sQuery(id+"F0.wireOp",EDGE,"E19.top"),sQuery(id+"F0.wireOp",EDGE,"E19.left"),sQuery(id+"F0.wireOp",EDGE,"E19.right"),sQuery(id+"F0.wireOp",EDGE,"E22"),sQuery(id+"F0.wireOp",EDGE,"E23"),sQuery(id+"F0.wireOp",EDGE,"E24"),sQuery(id+"F0.wireOp",EDGE,"E25"),sQuery(id+"F0.wireOp",EDGE,"E29"),sQuery(id+"F0.wireOp",EDGE,"E30"),sQuery(id+"F0.wireOp",EDGE,"E31"),sQuery(id+"F0.wireOp",EDGE,"E32"),sQuery(id+"F2.wireOp",EDGE,"E34.bottom"),sQuery(id+"F2.wireOp",EDGE,"E34.top"),sQuery(id+"F2.wireOp",EDGE,"E34.left"),sQuery(id+"F2.wireOp",EDGE,"E34.right"),sQuery(id+"F2.wireOp",EDGE,"E35.bottom"),sQuery(id+"F2.wireOp",EDGE,"E35.top"),sQuery(id+"F2.wireOp",EDGE,"E35.left"),sQuery(id+"F2.wireOp",EDGE,"E35.right")]),OD(3.0)]});
            var Q3;
            Q3=makeQuery(id+"F7.opShell","OFFSET_FACE",FACE,{"disambiguationData":[OSD([sQuery(id+"F0.wireOp",EDGE,"E0"),sQuery(id+"F0.wireOp",EDGE,"E1"),sQuery(id+"F0.wireOp",EDGE,"E2"),sQuery(id+"F0.wireOp",EDGE,"E3"),sQuery(id+"F0.wireOp",EDGE,"E7"),sQuery(id+"F0.wireOp",EDGE,"E8"),sQuery(id+"F0.wireOp",EDGE,"E9"),sQuery(id+"F0.wireOp",EDGE,"E10"),sQuery(id+"F0.wireOp",EDGE,"E11"),sQuery(id+"F0.wireOp",EDGE,"E12"),sQuery(id+"F0.wireOp",EDGE,"E14"),sQuery(id+"F0.wireOp",EDGE,"E15"),sQuery(id+"F0.wireOp",EDGE,"E19.bottom"),sQuery(id+"F0.wireOp",EDGE,"E19.top"),sQuery(id+"F0.wireOp",EDGE,"E19.left"),sQuery(id+"F0.wireOp",EDGE,"E19.right"),sQuery(id+"F0.wireOp",EDGE,"E22"),sQuery(id+"F0.wireOp",EDGE,"E23"),sQuery(id+"F0.wireOp",EDGE,"E24"),sQuery(id+"F0.wireOp",EDGE,"E25"),sQuery(id+"F0.wireOp",EDGE,"E29"),sQuery(id+"F0.wireOp",EDGE,"E30"),sQuery(id+"F0.wireOp",EDGE,"E31"),sQuery(id+"F0.wireOp",EDGE,"E32"),sQuery(id+"F2.wireOp",EDGE,"E34.bottom"),sQuery(id+"F2.wireOp",EDGE,"E34.top"),sQuery(id+"F2.wireOp",EDGE,"E34.left"),sQuery(id+"F2.wireOp",EDGE,"E34.right"),sQuery(id+"F2.wireOp",EDGE,"E35.bottom"),sQuery(id+"F2.wireOp",EDGE,"E35.top"),sQuery(id+"F2.wireOp",EDGE,"E35.left"),sQuery(id+"F2.wireOp",EDGE,"E35.right")]),OD(1.0)]});
            var Q4;
            Q4=makeQuery(id+"F3.boolean.opBoolean","MERGE",FACE,{"derivedFrom":[makeQuery(id+"F1.opExtrude","CAP_FACE",FACE,{"disambiguationData":[OSD([sQuery(id+"F0.wireOp",EDGE,"E0"),sQuery(id+"F0.wireOp",EDGE,"E1"),sQuery(id+"F0.wireOp",EDGE,"E2"),sQuery(id+"F0.wireOp",EDGE,"E3"),sQuery(id+"F0.wireOp",EDGE,"E7"),sQuery(id+"F0.wireOp",EDGE,"E8"),sQuery(id+"F0.wireOp",EDGE,"E9"),sQuery(id+"F0.wireOp",EDGE,"E10"),sQuery(id+"F0.wireOp",EDGE,"E11"),sQuery(id+"F0.wireOp",EDGE,"E12"),sQuery(id+"F0.wireOp",EDGE,"E14"),sQuery(id+"F0.wireOp",EDGE,"E15"),sQuery(id+"F0.wireOp",EDGE,"E19.bottom"),sQuery(id+"F0.wireOp",EDGE,"E19.top"),sQuery(id+"F0.wireOp",EDGE,"E19.left"),sQuery(id+"F0.wireOp",EDGE,"E19.right"),sQuery(id+"F0.wireOp",EDGE,"E22"),sQuery(id+"F0.wireOp",EDGE,"E23"),sQuery(id+"F0.wireOp",EDGE,"E24"),sQuery(id+"F0.wireOp",EDGE,"E25"),sQuery(id+"F0.wireOp",EDGE,"E29"),sQuery(id+"F0.wireOp",EDGE,"E30"),sQuery(id+"F0.wireOp",EDGE,"E31"),sQuery(id+"F0.wireOp",EDGE,"E32")])],"isStart":true}),makeQuery(id+"F3.opExtrude","CAP_FACE",FACE,{"disambiguationData":[OSD([sQuery(id+"F2.wireOp",EDGE,"E34.bottom"),sQuery(id+"F2.wireOp",EDGE,"E34.top"),sQuery(id+"F2.wireOp",EDGE,"E34.left"),sQuery(id+"F2.wireOp",EDGE,"E34.right")])],"isStart":true}),makeQuery(id+"F3.opExtrude","CAP_FACE",FACE,{"disambiguationData":[OSD([sQuery(id+"F2.wireOp",EDGE,"E35.bottom"),sQuery(id+"F2.wireOp",EDGE,"E35.top"),sQuery(id+"F2.wireOp",EDGE,"E35.left"),sQuery(id+"F2.wireOp",EDGE,"E35.right")])],"isStart":true})]});
            extrude(context, id + "F8", {"entities" : qUnion([Q0, Q1, Q2, Q3]), "operationType" : NewBodyOperationType.REMOVE, "endBound" : BoundingType.UP_TO_SURFACE, "oppositeDirection" : true, "endBoundEntityFace" : qUnion([Q4]), "depth" : 25.4 * mm});
        }
        {
            var Q0;
            {var subQ0=sQuery(id+"F2.wireOp",EDGE,"E35.right");var subQ1=sQuery(id+"F2.wireOp",EDGE,"E35.left");var subQ2=sQuery(id+"F2.wireOp",EDGE,"E35.top");var subQ3=sQuery(id+"F2.wireOp",EDGE,"E35.bottom");var subQ4=sQuery(id+"F2.wireOp",EDGE,"E34.right");var subQ5=sQuery(id+"F2.wireOp",EDGE,"E34.left");var subQ6=sQuery(id+"F2.wireOp",EDGE,"E34.top");var subQ7=sQuery(id+"F2.wireOp",EDGE,"E34.bottom");var subQ8=sQuery(id+"F0.wireOp",EDGE,"E32");var subQ9=sQuery(id+"F0.wireOp",EDGE,"E31");var subQ10=sQuery(id+"F0.wireOp",EDGE,"E30");var subQ11=sQuery(id+"F0.wireOp",EDGE,"E29");var subQ12=sQuery(id+"F0.wireOp",EDGE,"E25");var subQ13=sQuery(id+"F0.wireOp",EDGE,"E24");var subQ14=sQuery(id+"F0.wireOp",EDGE,"E23");var subQ15=sQuery(id+"F0.wireOp",EDGE,"E22");var subQ16=sQuery(id+"F0.wireOp",EDGE,"E19.right");var subQ17=sQuery(id+"F0.wireOp",EDGE,"E19.left");var subQ18=sQuery(id+"F0.wireOp",EDGE,"E19.top");var subQ19=sQuery(id+"F0.wireOp",EDGE,"E19.bottom");var subQ20=sQuery(id+"F0.wireOp",EDGE,"E15");var subQ21=sQuery(id+"F0.wireOp",EDGE,"E14");var subQ22=sQuery(id+"F0.wireOp",EDGE,"E12");var subQ23=sQuery(id+"F0.wireOp",EDGE,"E11");var subQ24=sQuery(id+"F0.wireOp",EDGE,"E10");var subQ25=sQuery(id+"F0.wireOp",EDGE,"E9");var subQ26=sQuery(id+"F0.wireOp",EDGE,"E8");var subQ27=sQuery(id+"F0.wireOp",EDGE,"E7");var subQ28=sQuery(id+"F0.wireOp",EDGE,"E3");var subQ29=sQuery(id+"F0.wireOp",EDGE,"E2");var subQ30=sQuery(id+"F0.wireOp",EDGE,"E1");var subQ31=sQuery(id+"F0.wireOp",EDGE,"E0");var subQ32=sQuery(id+"F5.wireOp",EDGE,"E41");var subQ33=makeQuery(id+"F6.boolean.opBoolean","COPY",FACE,{"derivedFrom":makeQuery(id+"F6.opExtrude","SWEPT_FACE",FACE,{"disambiguationData":[OSD([subQ32])]})});var subQ34=makeQuery(id+"F1.opExtrude","SWEPT_FACE",FACE,{"disambiguationData":[OSD([subQ31])]});Q0=makeQuery(id+"F8.boolean.opBoolean","MERGE",EDGE,{"derivedFrom":[makeQuery(id+"F7.opShell","TWEAK_EDGE",EDGE,{"derivedFrom":[subQ34,subQ33]}),makeQuery(id+"F8.opExtrude","SWEPT_EDGE",EDGE,{"disambiguationData":[OSD([subQ31,subQ30,subQ29,subQ28,subQ27,subQ26,subQ25,subQ24,subQ23,subQ22,subQ21,subQ20,subQ19,subQ18,subQ17,subQ16,subQ15,subQ14,subQ13,subQ12,subQ11,subQ10,subQ9,subQ8,subQ7,subQ6,subQ5,subQ4,subQ3,subQ2,subQ1,subQ0,subQ32]),TDD([makeQuery(id+"F7.opShell","TWEAK_VERTEX",VERTEX,{"derivedFrom":[subQ34,subQ33,makeQuery(id+"F3.boolean.opBoolean","MERGE",FACE,{"derivedFrom":[makeQuery(id+"F1.opExtrude","CAP_FACE",FACE,{"disambiguationData":[OSD([subQ31,subQ30,subQ29,subQ28,subQ27,subQ26,subQ25,subQ24,subQ23,subQ22,subQ21,subQ20,subQ19,subQ18,subQ17,subQ16,subQ15,subQ14,subQ13,subQ12,subQ11,subQ10,subQ9,subQ8])],"isStart":true}),makeQuery(id+"F3.opExtrude","CAP_FACE",FACE,{"disambiguationData":[OSD([subQ7,subQ6,subQ5,subQ4])],"isStart":true}),makeQuery(id+"F3.opExtrude","CAP_FACE",FACE,{"disambiguationData":[OSD([subQ3,subQ2,subQ1,subQ0])],"isStart":true})]})]})])]})]});}
            var Q1;
            {var subQ0=sQuery(id+"F2.wireOp",EDGE,"E35.right");var subQ1=sQuery(id+"F2.wireOp",EDGE,"E35.left");var subQ2=sQuery(id+"F2.wireOp",EDGE,"E35.top");var subQ3=sQuery(id+"F2.wireOp",EDGE,"E35.bottom");var subQ4=sQuery(id+"F2.wireOp",EDGE,"E34.right");var subQ5=sQuery(id+"F2.wireOp",EDGE,"E34.left");var subQ6=sQuery(id+"F2.wireOp",EDGE,"E34.top");var subQ7=sQuery(id+"F2.wireOp",EDGE,"E34.bottom");var subQ8=sQuery(id+"F0.wireOp",EDGE,"E32");var subQ9=sQuery(id+"F0.wireOp",EDGE,"E31");var subQ10=sQuery(id+"F0.wireOp",EDGE,"E30");var subQ11=sQuery(id+"F0.wireOp",EDGE,"E29");var subQ12=sQuery(id+"F0.wireOp",EDGE,"E25");var subQ13=sQuery(id+"F0.wireOp",EDGE,"E24");var subQ14=sQuery(id+"F0.wireOp",EDGE,"E23");var subQ15=sQuery(id+"F0.wireOp",EDGE,"E22");var subQ16=sQuery(id+"F0.wireOp",EDGE,"E19.right");var subQ17=sQuery(id+"F0.wireOp",EDGE,"E19.left");var subQ18=sQuery(id+"F0.wireOp",EDGE,"E19.top");var subQ19=sQuery(id+"F0.wireOp",EDGE,"E19.bottom");var subQ20=sQuery(id+"F0.wireOp",EDGE,"E15");var subQ21=sQuery(id+"F0.wireOp",EDGE,"E14");var subQ22=sQuery(id+"F0.wireOp",EDGE,"E12");var subQ23=sQuery(id+"F0.wireOp",EDGE,"E11");var subQ24=sQuery(id+"F0.wireOp",EDGE,"E10");var subQ25=sQuery(id+"F0.wireOp",EDGE,"E9");var subQ26=sQuery(id+"F0.wireOp",EDGE,"E8");var subQ27=sQuery(id+"F0.wireOp",EDGE,"E7");var subQ28=sQuery(id+"F0.wireOp",EDGE,"E3");var subQ29=sQuery(id+"F0.wireOp",EDGE,"E2");var subQ30=sQuery(id+"F0.wireOp",EDGE,"E1");var subQ31=sQuery(id+"F0.wireOp",EDGE,"E0");var subQ32=sQuery(id+"F5.wireOp",EDGE,"E41");var subQ33=makeQuery(id+"F6.boolean.opBoolean","COPY",FACE,{"derivedFrom":makeQuery(id+"F6.opExtrude","SWEPT_FACE",FACE,{"disambiguationData":[OSD([subQ32])]})});var subQ34=makeQuery(id+"F1.opExtrude","SWEPT_FACE",FACE,{"disambiguationData":[OSD([subQ16])]});Q1=makeQuery(id+"F8.boolean.opBoolean","MERGE",EDGE,{"derivedFrom":[makeQuery(id+"F7.opShell","TWEAK_EDGE",EDGE,{"derivedFrom":[subQ34,subQ33]}),makeQuery(id+"F8.opExtrude","SWEPT_EDGE",EDGE,{"disambiguationData":[OSD([subQ31,subQ30,subQ29,subQ28,subQ27,subQ26,subQ25,subQ24,subQ23,subQ22,subQ21,subQ20,subQ19,subQ18,subQ17,subQ16,subQ15,subQ14,subQ13,subQ12,subQ11,subQ10,subQ9,subQ8,subQ7,subQ6,subQ5,subQ4,subQ3,subQ2,subQ1,subQ0,subQ32]),TDD([makeQuery(id+"F7.opShell","TWEAK_VERTEX",VERTEX,{"derivedFrom":[subQ34,subQ33,makeQuery(id+"F3.boolean.opBoolean","MERGE",FACE,{"derivedFrom":[makeQuery(id+"F1.opExtrude","CAP_FACE",FACE,{"disambiguationData":[OSD([subQ31,subQ30,subQ29,subQ28,subQ27,subQ26,subQ25,subQ24,subQ23,subQ22,subQ21,subQ20,subQ19,subQ18,subQ17,subQ16,subQ15,subQ14,subQ13,subQ12,subQ11,subQ10,subQ9,subQ8])],"isStart":true}),makeQuery(id+"F3.opExtrude","CAP_FACE",FACE,{"disambiguationData":[OSD([subQ7,subQ6,subQ5,subQ4])],"isStart":true}),makeQuery(id+"F3.opExtrude","CAP_FACE",FACE,{"disambiguationData":[OSD([subQ3,subQ2,subQ1,subQ0])],"isStart":true})]})]})])]})]});}
            var Q2;
            {var subQ0=sQuery(id+"F2.wireOp",EDGE,"E35.right");var subQ1=sQuery(id+"F2.wireOp",EDGE,"E35.left");var subQ2=sQuery(id+"F2.wireOp",EDGE,"E35.top");var subQ3=sQuery(id+"F2.wireOp",EDGE,"E35.bottom");var subQ4=sQuery(id+"F2.wireOp",EDGE,"E34.right");var subQ5=sQuery(id+"F2.wireOp",EDGE,"E34.left");var subQ6=sQuery(id+"F2.wireOp",EDGE,"E34.top");var subQ7=sQuery(id+"F2.wireOp",EDGE,"E34.bottom");var subQ8=sQuery(id+"F0.wireOp",EDGE,"E32");var subQ9=sQuery(id+"F0.wireOp",EDGE,"E31");var subQ10=sQuery(id+"F0.wireOp",EDGE,"E30");var subQ11=sQuery(id+"F0.wireOp",EDGE,"E29");var subQ12=sQuery(id+"F0.wireOp",EDGE,"E25");var subQ13=sQuery(id+"F0.wireOp",EDGE,"E24");var subQ14=sQuery(id+"F0.wireOp",EDGE,"E23");var subQ15=sQuery(id+"F0.wireOp",EDGE,"E22");var subQ16=sQuery(id+"F0.wireOp",EDGE,"E19.right");var subQ17=sQuery(id+"F0.wireOp",EDGE,"E19.left");var subQ18=sQuery(id+"F0.wireOp",EDGE,"E19.top");var subQ19=sQuery(id+"F0.wireOp",EDGE,"E19.bottom");var subQ20=sQuery(id+"F0.wireOp",EDGE,"E15");var subQ21=sQuery(id+"F0.wireOp",EDGE,"E14");var subQ22=sQuery(id+"F0.wireOp",EDGE,"E12");var subQ23=sQuery(id+"F0.wireOp",EDGE,"E11");var subQ24=sQuery(id+"F0.wireOp",EDGE,"E10");var subQ25=sQuery(id+"F0.wireOp",EDGE,"E9");var subQ26=sQuery(id+"F0.wireOp",EDGE,"E8");var subQ27=sQuery(id+"F0.wireOp",EDGE,"E7");var subQ28=sQuery(id+"F0.wireOp",EDGE,"E3");var subQ29=sQuery(id+"F0.wireOp",EDGE,"E2");var subQ30=sQuery(id+"F0.wireOp",EDGE,"E1");var subQ31=sQuery(id+"F0.wireOp",EDGE,"E0");var subQ32=makeQuery(id+"F1.opExtrude","SWEPT_FACE",FACE,{"disambiguationData":[OSD([subQ19])]});var subQ33=makeQuery(id+"F4.opFillet","BLEND_FACE",FACE,{"disambiguationData":[OSD([subQ14,subQ13])]});Q2=makeQuery(id+"F8.boolean.opBoolean","MERGE",EDGE,{"derivedFrom":[makeQuery(id+"F7.opShell","TWEAK_EDGE",EDGE,{"derivedFrom":[subQ33,subQ32]}),makeQuery(id+"F8.opExtrude","SWEPT_EDGE",EDGE,{"disambiguationData":[OSD([subQ31,subQ30,subQ29,subQ28,subQ27,subQ26,subQ25,subQ24,subQ23,subQ22,subQ21,subQ20,subQ19,subQ18,subQ17,subQ16,subQ15,subQ14,subQ13,subQ12,subQ11,subQ10,subQ9,subQ8,subQ7,subQ6,subQ5,subQ4,subQ3,subQ2,subQ1,subQ0]),TDD([makeQuery(id+"F7.opShell","TWEAK_VERTEX",VERTEX,{"derivedFrom":[subQ33,subQ32,makeQuery(id+"F3.boolean.opBoolean","MERGE",FACE,{"derivedFrom":[makeQuery(id+"F1.opExtrude","CAP_FACE",FACE,{"disambiguationData":[OSD([subQ31,subQ30,subQ29,subQ28,subQ27,subQ26,subQ25,subQ24,subQ23,subQ22,subQ21,subQ20,subQ19,subQ18,subQ17,subQ16,subQ15,subQ14,subQ13,subQ12,subQ11,subQ10,subQ9,subQ8])],"isStart":true}),makeQuery(id+"F3.opExtrude","CAP_FACE",FACE,{"disambiguationData":[OSD([subQ7,subQ6,subQ5,subQ4])],"isStart":true}),makeQuery(id+"F3.opExtrude","CAP_FACE",FACE,{"disambiguationData":[OSD([subQ3,subQ2,subQ1,subQ0])],"isStart":true})]})]})])]})]});}
            var Q3;
            {var subQ0=sQuery(id+"F2.wireOp",EDGE,"E35.right");var subQ1=sQuery(id+"F2.wireOp",EDGE,"E35.left");var subQ2=sQuery(id+"F2.wireOp",EDGE,"E35.top");var subQ3=sQuery(id+"F2.wireOp",EDGE,"E35.bottom");var subQ4=sQuery(id+"F2.wireOp",EDGE,"E34.right");var subQ5=sQuery(id+"F2.wireOp",EDGE,"E34.left");var subQ6=sQuery(id+"F2.wireOp",EDGE,"E34.top");var subQ7=sQuery(id+"F2.wireOp",EDGE,"E34.bottom");var subQ8=sQuery(id+"F0.wireOp",EDGE,"E32");var subQ9=sQuery(id+"F0.wireOp",EDGE,"E31");var subQ10=sQuery(id+"F0.wireOp",EDGE,"E30");var subQ11=sQuery(id+"F0.wireOp",EDGE,"E29");var subQ12=sQuery(id+"F0.wireOp",EDGE,"E25");var subQ13=sQuery(id+"F0.wireOp",EDGE,"E24");var subQ14=sQuery(id+"F0.wireOp",EDGE,"E23");var subQ15=sQuery(id+"F0.wireOp",EDGE,"E22");var subQ16=sQuery(id+"F0.wireOp",EDGE,"E19.right");var subQ17=sQuery(id+"F0.wireOp",EDGE,"E19.left");var subQ18=sQuery(id+"F0.wireOp",EDGE,"E19.top");var subQ19=sQuery(id+"F0.wireOp",EDGE,"E19.bottom");var subQ20=sQuery(id+"F0.wireOp",EDGE,"E15");var subQ21=sQuery(id+"F0.wireOp",EDGE,"E14");var subQ22=sQuery(id+"F0.wireOp",EDGE,"E12");var subQ23=sQuery(id+"F0.wireOp",EDGE,"E11");var subQ24=sQuery(id+"F0.wireOp",EDGE,"E10");var subQ25=sQuery(id+"F0.wireOp",EDGE,"E9");var subQ26=sQuery(id+"F0.wireOp",EDGE,"E8");var subQ27=sQuery(id+"F0.wireOp",EDGE,"E7");var subQ28=sQuery(id+"F0.wireOp",EDGE,"E3");var subQ29=sQuery(id+"F0.wireOp",EDGE,"E2");var subQ30=sQuery(id+"F0.wireOp",EDGE,"E1");var subQ31=sQuery(id+"F0.wireOp",EDGE,"E0");var subQ32=makeQuery(id+"F1.opExtrude","SWEPT_FACE",FACE,{"disambiguationData":[OSD([subQ19])]});var subQ33=makeQuery(id+"F4.opFillet","BLEND_FACE",FACE,{"disambiguationData":[OSD([subQ15,subQ14])]});Q3=makeQuery(id+"F8.boolean.opBoolean","MERGE",EDGE,{"derivedFrom":[makeQuery(id+"F7.opShell","TWEAK_EDGE",EDGE,{"derivedFrom":[subQ33,subQ32]}),makeQuery(id+"F8.opExtrude","SWEPT_EDGE",EDGE,{"disambiguationData":[OSD([subQ31,subQ30,subQ29,subQ28,subQ27,subQ26,subQ25,subQ24,subQ23,subQ22,subQ21,subQ20,subQ19,subQ18,subQ17,subQ16,subQ15,subQ14,subQ13,subQ12,subQ11,subQ10,subQ9,subQ8,subQ7,subQ6,subQ5,subQ4,subQ3,subQ2,subQ1,subQ0]),TDD([makeQuery(id+"F7.opShell","TWEAK_VERTEX",VERTEX,{"derivedFrom":[subQ33,subQ32,makeQuery(id+"F3.boolean.opBoolean","MERGE",FACE,{"derivedFrom":[makeQuery(id+"F1.opExtrude","CAP_FACE",FACE,{"disambiguationData":[OSD([subQ31,subQ30,subQ29,subQ28,subQ27,subQ26,subQ25,subQ24,subQ23,subQ22,subQ21,subQ20,subQ19,subQ18,subQ17,subQ16,subQ15,subQ14,subQ13,subQ12,subQ11,subQ10,subQ9,subQ8])],"isStart":true}),makeQuery(id+"F3.opExtrude","CAP_FACE",FACE,{"disambiguationData":[OSD([subQ7,subQ6,subQ5,subQ4])],"isStart":true}),makeQuery(id+"F3.opExtrude","CAP_FACE",FACE,{"disambiguationData":[OSD([subQ3,subQ2,subQ1,subQ0])],"isStart":true})]})]})])]})]});}
            var Q4;
            {var subQ0=sQuery(id+"F2.wireOp",EDGE,"E35.right");var subQ1=sQuery(id+"F2.wireOp",EDGE,"E35.left");var subQ2=sQuery(id+"F2.wireOp",EDGE,"E35.top");var subQ3=sQuery(id+"F2.wireOp",EDGE,"E35.bottom");var subQ4=sQuery(id+"F2.wireOp",EDGE,"E34.right");var subQ5=sQuery(id+"F2.wireOp",EDGE,"E34.left");var subQ6=sQuery(id+"F2.wireOp",EDGE,"E34.top");var subQ7=sQuery(id+"F2.wireOp",EDGE,"E34.bottom");var subQ8=sQuery(id+"F0.wireOp",EDGE,"E32");var subQ9=sQuery(id+"F0.wireOp",EDGE,"E31");var subQ10=sQuery(id+"F0.wireOp",EDGE,"E30");var subQ11=sQuery(id+"F0.wireOp",EDGE,"E29");var subQ12=sQuery(id+"F0.wireOp",EDGE,"E25");var subQ13=sQuery(id+"F0.wireOp",EDGE,"E24");var subQ14=sQuery(id+"F0.wireOp",EDGE,"E23");var subQ15=sQuery(id+"F0.wireOp",EDGE,"E22");var subQ16=sQuery(id+"F0.wireOp",EDGE,"E19.right");var subQ17=sQuery(id+"F0.wireOp",EDGE,"E19.left");var subQ18=sQuery(id+"F0.wireOp",EDGE,"E19.top");var subQ19=sQuery(id+"F0.wireOp",EDGE,"E19.bottom");var subQ20=sQuery(id+"F0.wireOp",EDGE,"E15");var subQ21=sQuery(id+"F0.wireOp",EDGE,"E14");var subQ22=sQuery(id+"F0.wireOp",EDGE,"E12");var subQ23=sQuery(id+"F0.wireOp",EDGE,"E11");var subQ24=sQuery(id+"F0.wireOp",EDGE,"E10");var subQ25=sQuery(id+"F0.wireOp",EDGE,"E9");var subQ26=sQuery(id+"F0.wireOp",EDGE,"E8");var subQ27=sQuery(id+"F0.wireOp",EDGE,"E7");var subQ28=sQuery(id+"F0.wireOp",EDGE,"E3");var subQ29=sQuery(id+"F0.wireOp",EDGE,"E2");var subQ30=sQuery(id+"F0.wireOp",EDGE,"E1");var subQ31=sQuery(id+"F0.wireOp",EDGE,"E0");var subQ32=sQuery(id+"F5.wireOp",EDGE,"E37");var subQ33=makeQuery(id+"F6.boolean.opBoolean","COPY",FACE,{"derivedFrom":makeQuery(id+"F6.opExtrude","SWEPT_FACE",FACE,{"disambiguationData":[OSD([subQ32])]})});var subQ34=makeQuery(id+"F1.opExtrude","SWEPT_FACE",FACE,{"disambiguationData":[OSD([subQ12])]});Q4=makeQuery(id+"F8.boolean.opBoolean","MERGE",EDGE,{"derivedFrom":[makeQuery(id+"F7.opShell","TWEAK_EDGE",EDGE,{"derivedFrom":[subQ34,subQ33]}),makeQuery(id+"F8.opExtrude","SWEPT_EDGE",EDGE,{"disambiguationData":[OSD([subQ31,subQ30,subQ29,subQ28,subQ27,subQ26,subQ25,subQ24,subQ23,subQ22,subQ21,subQ20,subQ19,subQ18,subQ17,subQ16,subQ15,subQ14,subQ13,subQ12,subQ11,subQ10,subQ9,subQ8,subQ7,subQ6,subQ5,subQ4,subQ3,subQ2,subQ1,subQ0,subQ32]),TDD([makeQuery(id+"F7.opShell","TWEAK_VERTEX",VERTEX,{"derivedFrom":[subQ34,subQ33,makeQuery(id+"F3.boolean.opBoolean","MERGE",FACE,{"derivedFrom":[makeQuery(id+"F1.opExtrude","CAP_FACE",FACE,{"disambiguationData":[OSD([subQ31,subQ30,subQ29,subQ28,subQ27,subQ26,subQ25,subQ24,subQ23,subQ22,subQ21,subQ20,subQ19,subQ18,subQ17,subQ16,subQ15,subQ14,subQ13,subQ12,subQ11,subQ10,subQ9,subQ8])],"isStart":true}),makeQuery(id+"F3.opExtrude","CAP_FACE",FACE,{"disambiguationData":[OSD([subQ7,subQ6,subQ5,subQ4])],"isStart":true}),makeQuery(id+"F3.opExtrude","CAP_FACE",FACE,{"disambiguationData":[OSD([subQ3,subQ2,subQ1,subQ0])],"isStart":true})]})]})])]})]});}
            var Q5;
            {var subQ0=sQuery(id+"F2.wireOp",EDGE,"E35.right");var subQ1=sQuery(id+"F2.wireOp",EDGE,"E35.left");var subQ2=sQuery(id+"F2.wireOp",EDGE,"E35.top");var subQ3=sQuery(id+"F2.wireOp",EDGE,"E35.bottom");var subQ4=sQuery(id+"F2.wireOp",EDGE,"E34.right");var subQ5=sQuery(id+"F2.wireOp",EDGE,"E34.left");var subQ6=sQuery(id+"F2.wireOp",EDGE,"E34.top");var subQ7=sQuery(id+"F2.wireOp",EDGE,"E34.bottom");var subQ8=sQuery(id+"F0.wireOp",EDGE,"E32");var subQ9=sQuery(id+"F0.wireOp",EDGE,"E31");var subQ10=sQuery(id+"F0.wireOp",EDGE,"E30");var subQ11=sQuery(id+"F0.wireOp",EDGE,"E29");var subQ12=sQuery(id+"F0.wireOp",EDGE,"E25");var subQ13=sQuery(id+"F0.wireOp",EDGE,"E24");var subQ14=sQuery(id+"F0.wireOp",EDGE,"E23");var subQ15=sQuery(id+"F0.wireOp",EDGE,"E22");var subQ16=sQuery(id+"F0.wireOp",EDGE,"E19.right");var subQ17=sQuery(id+"F0.wireOp",EDGE,"E19.left");var subQ18=sQuery(id+"F0.wireOp",EDGE,"E19.top");var subQ19=sQuery(id+"F0.wireOp",EDGE,"E19.bottom");var subQ20=sQuery(id+"F0.wireOp",EDGE,"E15");var subQ21=sQuery(id+"F0.wireOp",EDGE,"E14");var subQ22=sQuery(id+"F0.wireOp",EDGE,"E12");var subQ23=sQuery(id+"F0.wireOp",EDGE,"E11");var subQ24=sQuery(id+"F0.wireOp",EDGE,"E10");var subQ25=sQuery(id+"F0.wireOp",EDGE,"E9");var subQ26=sQuery(id+"F0.wireOp",EDGE,"E8");var subQ27=sQuery(id+"F0.wireOp",EDGE,"E7");var subQ28=sQuery(id+"F0.wireOp",EDGE,"E3");var subQ29=sQuery(id+"F0.wireOp",EDGE,"E2");var subQ30=sQuery(id+"F0.wireOp",EDGE,"E1");var subQ31=sQuery(id+"F0.wireOp",EDGE,"E0");var subQ32=sQuery(id+"F5.wireOp",EDGE,"E37");var subQ33=makeQuery(id+"F6.boolean.opBoolean","COPY",FACE,{"derivedFrom":makeQuery(id+"F6.opExtrude","SWEPT_FACE",FACE,{"disambiguationData":[OSD([subQ32])]})});var subQ34=makeQuery(id+"F1.opExtrude","SWEPT_FACE",FACE,{"disambiguationData":[OSD([subQ17])]});Q5=makeQuery(id+"F8.boolean.opBoolean","MERGE",EDGE,{"derivedFrom":[makeQuery(id+"F7.opShell","TWEAK_EDGE",EDGE,{"derivedFrom":[subQ34,subQ33]}),makeQuery(id+"F8.opExtrude","SWEPT_EDGE",EDGE,{"disambiguationData":[OSD([subQ31,subQ30,subQ29,subQ28,subQ27,subQ26,subQ25,subQ24,subQ23,subQ22,subQ21,subQ20,subQ19,subQ18,subQ17,subQ16,subQ15,subQ14,subQ13,subQ12,subQ11,subQ10,subQ9,subQ8,subQ7,subQ6,subQ5,subQ4,subQ3,subQ2,subQ1,subQ0,subQ32]),TDD([makeQuery(id+"F7.opShell","TWEAK_VERTEX",VERTEX,{"derivedFrom":[subQ34,subQ33,makeQuery(id+"F3.boolean.opBoolean","MERGE",FACE,{"derivedFrom":[makeQuery(id+"F1.opExtrude","CAP_FACE",FACE,{"disambiguationData":[OSD([subQ31,subQ30,subQ29,subQ28,subQ27,subQ26,subQ25,subQ24,subQ23,subQ22,subQ21,subQ20,subQ19,subQ18,subQ17,subQ16,subQ15,subQ14,subQ13,subQ12,subQ11,subQ10,subQ9,subQ8])],"isStart":true}),makeQuery(id+"F3.opExtrude","CAP_FACE",FACE,{"disambiguationData":[OSD([subQ7,subQ6,subQ5,subQ4])],"isStart":true}),makeQuery(id+"F3.opExtrude","CAP_FACE",FACE,{"disambiguationData":[OSD([subQ3,subQ2,subQ1,subQ0])],"isStart":true})]})]})])]})]});}
            var Q6;
            {var subQ0=sQuery(id+"F2.wireOp",EDGE,"E35.right");var subQ1=sQuery(id+"F2.wireOp",EDGE,"E35.left");var subQ2=sQuery(id+"F2.wireOp",EDGE,"E35.top");var subQ3=sQuery(id+"F2.wireOp",EDGE,"E35.bottom");var subQ4=sQuery(id+"F2.wireOp",EDGE,"E34.right");var subQ5=sQuery(id+"F2.wireOp",EDGE,"E34.left");var subQ6=sQuery(id+"F2.wireOp",EDGE,"E34.top");var subQ7=sQuery(id+"F2.wireOp",EDGE,"E34.bottom");var subQ8=sQuery(id+"F0.wireOp",EDGE,"E32");var subQ9=sQuery(id+"F0.wireOp",EDGE,"E31");var subQ10=sQuery(id+"F0.wireOp",EDGE,"E30");var subQ11=sQuery(id+"F0.wireOp",EDGE,"E29");var subQ12=sQuery(id+"F0.wireOp",EDGE,"E25");var subQ13=sQuery(id+"F0.wireOp",EDGE,"E24");var subQ14=sQuery(id+"F0.wireOp",EDGE,"E23");var subQ15=sQuery(id+"F0.wireOp",EDGE,"E22");var subQ16=sQuery(id+"F0.wireOp",EDGE,"E19.right");var subQ17=sQuery(id+"F0.wireOp",EDGE,"E19.left");var subQ18=sQuery(id+"F0.wireOp",EDGE,"E19.top");var subQ19=sQuery(id+"F0.wireOp",EDGE,"E19.bottom");var subQ20=sQuery(id+"F0.wireOp",EDGE,"E15");var subQ21=sQuery(id+"F0.wireOp",EDGE,"E14");var subQ22=sQuery(id+"F0.wireOp",EDGE,"E12");var subQ23=sQuery(id+"F0.wireOp",EDGE,"E11");var subQ24=sQuery(id+"F0.wireOp",EDGE,"E10");var subQ25=sQuery(id+"F0.wireOp",EDGE,"E9");var subQ26=sQuery(id+"F0.wireOp",EDGE,"E8");var subQ27=sQuery(id+"F0.wireOp",EDGE,"E7");var subQ28=sQuery(id+"F0.wireOp",EDGE,"E3");var subQ29=sQuery(id+"F0.wireOp",EDGE,"E2");var subQ30=sQuery(id+"F0.wireOp",EDGE,"E1");var subQ31=sQuery(id+"F0.wireOp",EDGE,"E0");var subQ32=sQuery(id+"F5.wireOp",EDGE,"E42");var subQ33=makeQuery(id+"F6.boolean.opBoolean","COPY",FACE,{"derivedFrom":makeQuery(id+"F6.opExtrude","SWEPT_FACE",FACE,{"disambiguationData":[OSD([subQ32])]})});var subQ34=makeQuery(id+"F1.opExtrude","SWEPT_FACE",FACE,{"disambiguationData":[OSD([subQ8])]});Q6=makeQuery(id+"F8.boolean.opBoolean","MERGE",EDGE,{"derivedFrom":[makeQuery(id+"F7.opShell","TWEAK_EDGE",EDGE,{"derivedFrom":[subQ34,subQ33]}),makeQuery(id+"F8.opExtrude","SWEPT_EDGE",EDGE,{"disambiguationData":[OSD([subQ31,subQ30,subQ29,subQ28,subQ27,subQ26,subQ25,subQ24,subQ23,subQ22,subQ21,subQ20,subQ19,subQ18,subQ17,subQ16,subQ15,subQ14,subQ13,subQ12,subQ11,subQ10,subQ9,subQ8,subQ7,subQ6,subQ5,subQ4,subQ3,subQ2,subQ1,subQ0,subQ32]),TDD([makeQuery(id+"F7.opShell","TWEAK_VERTEX",VERTEX,{"derivedFrom":[subQ34,subQ33,makeQuery(id+"F3.boolean.opBoolean","MERGE",FACE,{"derivedFrom":[makeQuery(id+"F1.opExtrude","CAP_FACE",FACE,{"disambiguationData":[OSD([subQ31,subQ30,subQ29,subQ28,subQ27,subQ26,subQ25,subQ24,subQ23,subQ22,subQ21,subQ20,subQ19,subQ18,subQ17,subQ16,subQ15,subQ14,subQ13,subQ12,subQ11,subQ10,subQ9,subQ8])],"isStart":true}),makeQuery(id+"F3.opExtrude","CAP_FACE",FACE,{"disambiguationData":[OSD([subQ7,subQ6,subQ5,subQ4])],"isStart":true}),makeQuery(id+"F3.opExtrude","CAP_FACE",FACE,{"disambiguationData":[OSD([subQ3,subQ2,subQ1,subQ0])],"isStart":true})]})]})])]})]});}
            var Q7;
            {var subQ0=sQuery(id+"F2.wireOp",EDGE,"E35.right");var subQ1=sQuery(id+"F2.wireOp",EDGE,"E35.left");var subQ2=sQuery(id+"F2.wireOp",EDGE,"E35.top");var subQ3=sQuery(id+"F2.wireOp",EDGE,"E35.bottom");var subQ4=sQuery(id+"F2.wireOp",EDGE,"E34.right");var subQ5=sQuery(id+"F2.wireOp",EDGE,"E34.left");var subQ6=sQuery(id+"F2.wireOp",EDGE,"E34.top");var subQ7=sQuery(id+"F2.wireOp",EDGE,"E34.bottom");var subQ8=sQuery(id+"F0.wireOp",EDGE,"E32");var subQ9=sQuery(id+"F0.wireOp",EDGE,"E31");var subQ10=sQuery(id+"F0.wireOp",EDGE,"E30");var subQ11=sQuery(id+"F0.wireOp",EDGE,"E29");var subQ12=sQuery(id+"F0.wireOp",EDGE,"E25");var subQ13=sQuery(id+"F0.wireOp",EDGE,"E24");var subQ14=sQuery(id+"F0.wireOp",EDGE,"E23");var subQ15=sQuery(id+"F0.wireOp",EDGE,"E22");var subQ16=sQuery(id+"F0.wireOp",EDGE,"E19.right");var subQ17=sQuery(id+"F0.wireOp",EDGE,"E19.left");var subQ18=sQuery(id+"F0.wireOp",EDGE,"E19.top");var subQ19=sQuery(id+"F0.wireOp",EDGE,"E19.bottom");var subQ20=sQuery(id+"F0.wireOp",EDGE,"E15");var subQ21=sQuery(id+"F0.wireOp",EDGE,"E14");var subQ22=sQuery(id+"F0.wireOp",EDGE,"E12");var subQ23=sQuery(id+"F0.wireOp",EDGE,"E11");var subQ24=sQuery(id+"F0.wireOp",EDGE,"E10");var subQ25=sQuery(id+"F0.wireOp",EDGE,"E9");var subQ26=sQuery(id+"F0.wireOp",EDGE,"E8");var subQ27=sQuery(id+"F0.wireOp",EDGE,"E7");var subQ28=sQuery(id+"F0.wireOp",EDGE,"E3");var subQ29=sQuery(id+"F0.wireOp",EDGE,"E2");var subQ30=sQuery(id+"F0.wireOp",EDGE,"E1");var subQ31=sQuery(id+"F0.wireOp",EDGE,"E0");var subQ32=sQuery(id+"F5.wireOp",EDGE,"E42");var subQ33=makeQuery(id+"F6.boolean.opBoolean","COPY",FACE,{"derivedFrom":makeQuery(id+"F6.opExtrude","SWEPT_FACE",FACE,{"disambiguationData":[OSD([subQ32])]})});var subQ34=makeQuery(id+"F1.opExtrude","SWEPT_FACE",FACE,{"disambiguationData":[OSD([subQ16])]});Q7=makeQuery(id+"F8.boolean.opBoolean","MERGE",EDGE,{"derivedFrom":[makeQuery(id+"F7.opShell","TWEAK_EDGE",EDGE,{"derivedFrom":[subQ34,subQ33]}),makeQuery(id+"F8.opExtrude","SWEPT_EDGE",EDGE,{"disambiguationData":[OSD([subQ31,subQ30,subQ29,subQ28,subQ27,subQ26,subQ25,subQ24,subQ23,subQ22,subQ21,subQ20,subQ19,subQ18,subQ17,subQ16,subQ15,subQ14,subQ13,subQ12,subQ11,subQ10,subQ9,subQ8,subQ7,subQ6,subQ5,subQ4,subQ3,subQ2,subQ1,subQ0,subQ32]),TDD([makeQuery(id+"F7.opShell","TWEAK_VERTEX",VERTEX,{"derivedFrom":[subQ34,subQ33,makeQuery(id+"F3.boolean.opBoolean","MERGE",FACE,{"derivedFrom":[makeQuery(id+"F1.opExtrude","CAP_FACE",FACE,{"disambiguationData":[OSD([subQ31,subQ30,subQ29,subQ28,subQ27,subQ26,subQ25,subQ24,subQ23,subQ22,subQ21,subQ20,subQ19,subQ18,subQ17,subQ16,subQ15,subQ14,subQ13,subQ12,subQ11,subQ10,subQ9,subQ8])],"isStart":true}),makeQuery(id+"F3.opExtrude","CAP_FACE",FACE,{"disambiguationData":[OSD([subQ7,subQ6,subQ5,subQ4])],"isStart":true}),makeQuery(id+"F3.opExtrude","CAP_FACE",FACE,{"disambiguationData":[OSD([subQ3,subQ2,subQ1,subQ0])],"isStart":true})]})]})])]})]});}
            var Q8;
            {var subQ0=sQuery(id+"F2.wireOp",EDGE,"E35.right");var subQ1=sQuery(id+"F2.wireOp",EDGE,"E35.left");var subQ2=sQuery(id+"F2.wireOp",EDGE,"E35.top");var subQ3=sQuery(id+"F2.wireOp",EDGE,"E35.bottom");var subQ4=sQuery(id+"F2.wireOp",EDGE,"E34.right");var subQ5=sQuery(id+"F2.wireOp",EDGE,"E34.left");var subQ6=sQuery(id+"F2.wireOp",EDGE,"E34.top");var subQ7=sQuery(id+"F2.wireOp",EDGE,"E34.bottom");var subQ8=sQuery(id+"F0.wireOp",EDGE,"E32");var subQ9=sQuery(id+"F0.wireOp",EDGE,"E31");var subQ10=sQuery(id+"F0.wireOp",EDGE,"E30");var subQ11=sQuery(id+"F0.wireOp",EDGE,"E29");var subQ12=sQuery(id+"F0.wireOp",EDGE,"E25");var subQ13=sQuery(id+"F0.wireOp",EDGE,"E24");var subQ14=sQuery(id+"F0.wireOp",EDGE,"E23");var subQ15=sQuery(id+"F0.wireOp",EDGE,"E22");var subQ16=sQuery(id+"F0.wireOp",EDGE,"E19.right");var subQ17=sQuery(id+"F0.wireOp",EDGE,"E19.left");var subQ18=sQuery(id+"F0.wireOp",EDGE,"E19.top");var subQ19=sQuery(id+"F0.wireOp",EDGE,"E19.bottom");var subQ20=sQuery(id+"F0.wireOp",EDGE,"E15");var subQ21=sQuery(id+"F0.wireOp",EDGE,"E14");var subQ22=sQuery(id+"F0.wireOp",EDGE,"E12");var subQ23=sQuery(id+"F0.wireOp",EDGE,"E11");var subQ24=sQuery(id+"F0.wireOp",EDGE,"E10");var subQ25=sQuery(id+"F0.wireOp",EDGE,"E9");var subQ26=sQuery(id+"F0.wireOp",EDGE,"E8");var subQ27=sQuery(id+"F0.wireOp",EDGE,"E7");var subQ28=sQuery(id+"F0.wireOp",EDGE,"E3");var subQ29=sQuery(id+"F0.wireOp",EDGE,"E2");var subQ30=sQuery(id+"F0.wireOp",EDGE,"E1");var subQ31=sQuery(id+"F0.wireOp",EDGE,"E0");var subQ32=sQuery(id+"F5.wireOp",EDGE,"E43");var subQ33=makeQuery(id+"F6.boolean.opBoolean","COPY",FACE,{"derivedFrom":makeQuery(id+"F6.opExtrude","SWEPT_FACE",FACE,{"disambiguationData":[OSD([subQ32])]})});var subQ34=makeQuery(id+"F1.opExtrude","SWEPT_FACE",FACE,{"disambiguationData":[OSD([subQ30])]});Q8=makeQuery(id+"F8.boolean.opBoolean","MERGE",EDGE,{"derivedFrom":[makeQuery(id+"F7.opShell","TWEAK_EDGE",EDGE,{"derivedFrom":[subQ34,subQ33]}),makeQuery(id+"F8.opExtrude","SWEPT_EDGE",EDGE,{"disambiguationData":[OSD([subQ31,subQ30,subQ29,subQ28,subQ27,subQ26,subQ25,subQ24,subQ23,subQ22,subQ21,subQ20,subQ19,subQ18,subQ17,subQ16,subQ15,subQ14,subQ13,subQ12,subQ11,subQ10,subQ9,subQ8,subQ7,subQ6,subQ5,subQ4,subQ3,subQ2,subQ1,subQ0,subQ32]),TDD([makeQuery(id+"F7.opShell","TWEAK_VERTEX",VERTEX,{"derivedFrom":[subQ34,subQ33,makeQuery(id+"F3.boolean.opBoolean","MERGE",FACE,{"derivedFrom":[makeQuery(id+"F1.opExtrude","CAP_FACE",FACE,{"disambiguationData":[OSD([subQ31,subQ30,subQ29,subQ28,subQ27,subQ26,subQ25,subQ24,subQ23,subQ22,subQ21,subQ20,subQ19,subQ18,subQ17,subQ16,subQ15,subQ14,subQ13,subQ12,subQ11,subQ10,subQ9,subQ8])],"isStart":true}),makeQuery(id+"F3.opExtrude","CAP_FACE",FACE,{"disambiguationData":[OSD([subQ7,subQ6,subQ5,subQ4])],"isStart":true}),makeQuery(id+"F3.opExtrude","CAP_FACE",FACE,{"disambiguationData":[OSD([subQ3,subQ2,subQ1,subQ0])],"isStart":true})]})]})])]})]});}
            var Q9;
            {var subQ0=sQuery(id+"F2.wireOp",EDGE,"E35.right");var subQ1=sQuery(id+"F2.wireOp",EDGE,"E35.left");var subQ2=sQuery(id+"F2.wireOp",EDGE,"E35.top");var subQ3=sQuery(id+"F2.wireOp",EDGE,"E35.bottom");var subQ4=sQuery(id+"F2.wireOp",EDGE,"E34.right");var subQ5=sQuery(id+"F2.wireOp",EDGE,"E34.left");var subQ6=sQuery(id+"F2.wireOp",EDGE,"E34.top");var subQ7=sQuery(id+"F2.wireOp",EDGE,"E34.bottom");var subQ8=sQuery(id+"F0.wireOp",EDGE,"E32");var subQ9=sQuery(id+"F0.wireOp",EDGE,"E31");var subQ10=sQuery(id+"F0.wireOp",EDGE,"E30");var subQ11=sQuery(id+"F0.wireOp",EDGE,"E29");var subQ12=sQuery(id+"F0.wireOp",EDGE,"E25");var subQ13=sQuery(id+"F0.wireOp",EDGE,"E24");var subQ14=sQuery(id+"F0.wireOp",EDGE,"E23");var subQ15=sQuery(id+"F0.wireOp",EDGE,"E22");var subQ16=sQuery(id+"F0.wireOp",EDGE,"E19.right");var subQ17=sQuery(id+"F0.wireOp",EDGE,"E19.left");var subQ18=sQuery(id+"F0.wireOp",EDGE,"E19.top");var subQ19=sQuery(id+"F0.wireOp",EDGE,"E19.bottom");var subQ20=sQuery(id+"F0.wireOp",EDGE,"E15");var subQ21=sQuery(id+"F0.wireOp",EDGE,"E14");var subQ22=sQuery(id+"F0.wireOp",EDGE,"E12");var subQ23=sQuery(id+"F0.wireOp",EDGE,"E11");var subQ24=sQuery(id+"F0.wireOp",EDGE,"E10");var subQ25=sQuery(id+"F0.wireOp",EDGE,"E9");var subQ26=sQuery(id+"F0.wireOp",EDGE,"E8");var subQ27=sQuery(id+"F0.wireOp",EDGE,"E7");var subQ28=sQuery(id+"F0.wireOp",EDGE,"E3");var subQ29=sQuery(id+"F0.wireOp",EDGE,"E2");var subQ30=sQuery(id+"F0.wireOp",EDGE,"E1");var subQ31=sQuery(id+"F0.wireOp",EDGE,"E0");var subQ32=sQuery(id+"F5.wireOp",EDGE,"E43");var subQ33=makeQuery(id+"F6.boolean.opBoolean","COPY",FACE,{"derivedFrom":makeQuery(id+"F6.opExtrude","SWEPT_FACE",FACE,{"disambiguationData":[OSD([subQ32])]})});var subQ34=makeQuery(id+"F1.opExtrude","SWEPT_FACE",FACE,{"disambiguationData":[OSD([subQ17])]});Q9=makeQuery(id+"F8.boolean.opBoolean","MERGE",EDGE,{"derivedFrom":[makeQuery(id+"F7.opShell","TWEAK_EDGE",EDGE,{"derivedFrom":[subQ34,subQ33]}),makeQuery(id+"F8.opExtrude","SWEPT_EDGE",EDGE,{"disambiguationData":[OSD([subQ31,subQ30,subQ29,subQ28,subQ27,subQ26,subQ25,subQ24,subQ23,subQ22,subQ21,subQ20,subQ19,subQ18,subQ17,subQ16,subQ15,subQ14,subQ13,subQ12,subQ11,subQ10,subQ9,subQ8,subQ7,subQ6,subQ5,subQ4,subQ3,subQ2,subQ1,subQ0,subQ32]),TDD([makeQuery(id+"F7.opShell","TWEAK_VERTEX",VERTEX,{"derivedFrom":[subQ34,subQ33,makeQuery(id+"F3.boolean.opBoolean","MERGE",FACE,{"derivedFrom":[makeQuery(id+"F1.opExtrude","CAP_FACE",FACE,{"disambiguationData":[OSD([subQ31,subQ30,subQ29,subQ28,subQ27,subQ26,subQ25,subQ24,subQ23,subQ22,subQ21,subQ20,subQ19,subQ18,subQ17,subQ16,subQ15,subQ14,subQ13,subQ12,subQ11,subQ10,subQ9,subQ8])],"isStart":true}),makeQuery(id+"F3.opExtrude","CAP_FACE",FACE,{"disambiguationData":[OSD([subQ7,subQ6,subQ5,subQ4])],"isStart":true}),makeQuery(id+"F3.opExtrude","CAP_FACE",FACE,{"disambiguationData":[OSD([subQ3,subQ2,subQ1,subQ0])],"isStart":true})]})]})])]})]});}
            var Q10;
            {var subQ0=sQuery(id+"F2.wireOp",EDGE,"E35.right");var subQ1=sQuery(id+"F2.wireOp",EDGE,"E35.left");var subQ2=sQuery(id+"F2.wireOp",EDGE,"E35.top");var subQ3=sQuery(id+"F2.wireOp",EDGE,"E35.bottom");var subQ4=sQuery(id+"F2.wireOp",EDGE,"E34.right");var subQ5=sQuery(id+"F2.wireOp",EDGE,"E34.left");var subQ6=sQuery(id+"F2.wireOp",EDGE,"E34.top");var subQ7=sQuery(id+"F2.wireOp",EDGE,"E34.bottom");var subQ8=sQuery(id+"F0.wireOp",EDGE,"E32");var subQ9=sQuery(id+"F0.wireOp",EDGE,"E31");var subQ10=sQuery(id+"F0.wireOp",EDGE,"E30");var subQ11=sQuery(id+"F0.wireOp",EDGE,"E29");var subQ12=sQuery(id+"F0.wireOp",EDGE,"E25");var subQ13=sQuery(id+"F0.wireOp",EDGE,"E24");var subQ14=sQuery(id+"F0.wireOp",EDGE,"E23");var subQ15=sQuery(id+"F0.wireOp",EDGE,"E22");var subQ16=sQuery(id+"F0.wireOp",EDGE,"E19.right");var subQ17=sQuery(id+"F0.wireOp",EDGE,"E19.left");var subQ18=sQuery(id+"F0.wireOp",EDGE,"E19.top");var subQ19=sQuery(id+"F0.wireOp",EDGE,"E19.bottom");var subQ20=sQuery(id+"F0.wireOp",EDGE,"E15");var subQ21=sQuery(id+"F0.wireOp",EDGE,"E14");var subQ22=sQuery(id+"F0.wireOp",EDGE,"E12");var subQ23=sQuery(id+"F0.wireOp",EDGE,"E11");var subQ24=sQuery(id+"F0.wireOp",EDGE,"E10");var subQ25=sQuery(id+"F0.wireOp",EDGE,"E9");var subQ26=sQuery(id+"F0.wireOp",EDGE,"E8");var subQ27=sQuery(id+"F0.wireOp",EDGE,"E7");var subQ28=sQuery(id+"F0.wireOp",EDGE,"E3");var subQ29=sQuery(id+"F0.wireOp",EDGE,"E2");var subQ30=sQuery(id+"F0.wireOp",EDGE,"E1");var subQ31=sQuery(id+"F0.wireOp",EDGE,"E0");var subQ32=makeQuery(id+"F1.opExtrude","SWEPT_FACE",FACE,{"disambiguationData":[OSD([subQ18])]});var subQ33=makeQuery(id+"F4.opFillet","BLEND_FACE",FACE,{"disambiguationData":[OSD([subQ11,subQ10])]});Q10=makeQuery(id+"F8.boolean.opBoolean","MERGE",EDGE,{"derivedFrom":[makeQuery(id+"F7.opShell","TWEAK_EDGE",EDGE,{"derivedFrom":[subQ33,subQ32]}),makeQuery(id+"F8.opExtrude","SWEPT_EDGE",EDGE,{"disambiguationData":[OSD([subQ31,subQ30,subQ29,subQ28,subQ27,subQ26,subQ25,subQ24,subQ23,subQ22,subQ21,subQ20,subQ19,subQ18,subQ17,subQ16,subQ15,subQ14,subQ13,subQ12,subQ11,subQ10,subQ9,subQ8,subQ7,subQ6,subQ5,subQ4,subQ3,subQ2,subQ1,subQ0]),TDD([makeQuery(id+"F7.opShell","TWEAK_VERTEX",VERTEX,{"derivedFrom":[subQ33,subQ32,makeQuery(id+"F3.boolean.opBoolean","MERGE",FACE,{"derivedFrom":[makeQuery(id+"F1.opExtrude","CAP_FACE",FACE,{"disambiguationData":[OSD([subQ31,subQ30,subQ29,subQ28,subQ27,subQ26,subQ25,subQ24,subQ23,subQ22,subQ21,subQ20,subQ19,subQ18,subQ17,subQ16,subQ15,subQ14,subQ13,subQ12,subQ11,subQ10,subQ9,subQ8])],"isStart":true}),makeQuery(id+"F3.opExtrude","CAP_FACE",FACE,{"disambiguationData":[OSD([subQ7,subQ6,subQ5,subQ4])],"isStart":true}),makeQuery(id+"F3.opExtrude","CAP_FACE",FACE,{"disambiguationData":[OSD([subQ3,subQ2,subQ1,subQ0])],"isStart":true})]})]})])]})]});}
            var Q11;
            {var subQ0=sQuery(id+"F2.wireOp",EDGE,"E35.right");var subQ1=sQuery(id+"F2.wireOp",EDGE,"E35.left");var subQ2=sQuery(id+"F2.wireOp",EDGE,"E35.top");var subQ3=sQuery(id+"F2.wireOp",EDGE,"E35.bottom");var subQ4=sQuery(id+"F2.wireOp",EDGE,"E34.right");var subQ5=sQuery(id+"F2.wireOp",EDGE,"E34.left");var subQ6=sQuery(id+"F2.wireOp",EDGE,"E34.top");var subQ7=sQuery(id+"F2.wireOp",EDGE,"E34.bottom");var subQ8=sQuery(id+"F0.wireOp",EDGE,"E32");var subQ9=sQuery(id+"F0.wireOp",EDGE,"E31");var subQ10=sQuery(id+"F0.wireOp",EDGE,"E30");var subQ11=sQuery(id+"F0.wireOp",EDGE,"E29");var subQ12=sQuery(id+"F0.wireOp",EDGE,"E25");var subQ13=sQuery(id+"F0.wireOp",EDGE,"E24");var subQ14=sQuery(id+"F0.wireOp",EDGE,"E23");var subQ15=sQuery(id+"F0.wireOp",EDGE,"E22");var subQ16=sQuery(id+"F0.wireOp",EDGE,"E19.right");var subQ17=sQuery(id+"F0.wireOp",EDGE,"E19.left");var subQ18=sQuery(id+"F0.wireOp",EDGE,"E19.top");var subQ19=sQuery(id+"F0.wireOp",EDGE,"E19.bottom");var subQ20=sQuery(id+"F0.wireOp",EDGE,"E15");var subQ21=sQuery(id+"F0.wireOp",EDGE,"E14");var subQ22=sQuery(id+"F0.wireOp",EDGE,"E12");var subQ23=sQuery(id+"F0.wireOp",EDGE,"E11");var subQ24=sQuery(id+"F0.wireOp",EDGE,"E10");var subQ25=sQuery(id+"F0.wireOp",EDGE,"E9");var subQ26=sQuery(id+"F0.wireOp",EDGE,"E8");var subQ27=sQuery(id+"F0.wireOp",EDGE,"E7");var subQ28=sQuery(id+"F0.wireOp",EDGE,"E3");var subQ29=sQuery(id+"F0.wireOp",EDGE,"E2");var subQ30=sQuery(id+"F0.wireOp",EDGE,"E1");var subQ31=sQuery(id+"F0.wireOp",EDGE,"E0");var subQ32=makeQuery(id+"F1.opExtrude","SWEPT_FACE",FACE,{"disambiguationData":[OSD([subQ18])]});var subQ33=makeQuery(id+"F4.opFillet","BLEND_FACE",FACE,{"disambiguationData":[OSD([subQ10,subQ9])]});Q11=makeQuery(id+"F8.boolean.opBoolean","MERGE",EDGE,{"derivedFrom":[makeQuery(id+"F7.opShell","TWEAK_EDGE",EDGE,{"derivedFrom":[subQ33,subQ32]}),makeQuery(id+"F8.opExtrude","SWEPT_EDGE",EDGE,{"disambiguationData":[OSD([subQ31,subQ30,subQ29,subQ28,subQ27,subQ26,subQ25,subQ24,subQ23,subQ22,subQ21,subQ20,subQ19,subQ18,subQ17,subQ16,subQ15,subQ14,subQ13,subQ12,subQ11,subQ10,subQ9,subQ8,subQ7,subQ6,subQ5,subQ4,subQ3,subQ2,subQ1,subQ0]),TDD([makeQuery(id+"F7.opShell","TWEAK_VERTEX",VERTEX,{"derivedFrom":[subQ33,subQ32,makeQuery(id+"F3.boolean.opBoolean","MERGE",FACE,{"derivedFrom":[makeQuery(id+"F1.opExtrude","CAP_FACE",FACE,{"disambiguationData":[OSD([subQ31,subQ30,subQ29,subQ28,subQ27,subQ26,subQ25,subQ24,subQ23,subQ22,subQ21,subQ20,subQ19,subQ18,subQ17,subQ16,subQ15,subQ14,subQ13,subQ12,subQ11,subQ10,subQ9,subQ8])],"isStart":true}),makeQuery(id+"F3.opExtrude","CAP_FACE",FACE,{"disambiguationData":[OSD([subQ7,subQ6,subQ5,subQ4])],"isStart":true}),makeQuery(id+"F3.opExtrude","CAP_FACE",FACE,{"disambiguationData":[OSD([subQ3,subQ2,subQ1,subQ0])],"isStart":true})]})]})])]})]});}
            fillet(context, id + "F9", {"entities" : qUnion([Q0, Q1, Q2, Q3, Q4, Q5, Q6, Q7, Q8, Q9, Q10, Q11]), "radius" : 1.27 * mm, "tangentPropagation" : true, "allowEdgeOverflow" : false});
        }
        {
            var Q0;
            Q0=makeQuery(id+"F3.boolean.opBoolean","MERGE",FACE,{"derivedFrom":[makeQuery(id+"F1.opExtrude","CAP_FACE",FACE,{"disambiguationData":[OSD([sQuery(id+"F0.wireOp",EDGE,"E0"),sQuery(id+"F0.wireOp",EDGE,"E1"),sQuery(id+"F0.wireOp",EDGE,"E2"),sQuery(id+"F0.wireOp",EDGE,"E3"),sQuery(id+"F0.wireOp",EDGE,"E7"),sQuery(id+"F0.wireOp",EDGE,"E8"),sQuery(id+"F0.wireOp",EDGE,"E9"),sQuery(id+"F0.wireOp",EDGE,"E10"),sQuery(id+"F0.wireOp",EDGE,"E11"),sQuery(id+"F0.wireOp",EDGE,"E12"),sQuery(id+"F0.wireOp",EDGE,"E14"),sQuery(id+"F0.wireOp",EDGE,"E15"),sQuery(id+"F0.wireOp",EDGE,"E19.bottom"),sQuery(id+"F0.wireOp",EDGE,"E19.top"),sQuery(id+"F0.wireOp",EDGE,"E19.left"),sQuery(id+"F0.wireOp",EDGE,"E19.right"),sQuery(id+"F0.wireOp",EDGE,"E22"),sQuery(id+"F0.wireOp",EDGE,"E23"),sQuery(id+"F0.wireOp",EDGE,"E24"),sQuery(id+"F0.wireOp",EDGE,"E25"),sQuery(id+"F0.wireOp",EDGE,"E29"),sQuery(id+"F0.wireOp",EDGE,"E30"),sQuery(id+"F0.wireOp",EDGE,"E31"),sQuery(id+"F0.wireOp",EDGE,"E32")])],"isStart":true}),makeQuery(id+"F3.opExtrude","CAP_FACE",FACE,{"disambiguationData":[OSD([sQuery(id+"F2.wireOp",EDGE,"E34.bottom"),sQuery(id+"F2.wireOp",EDGE,"E34.top"),sQuery(id+"F2.wireOp",EDGE,"E34.left"),sQuery(id+"F2.wireOp",EDGE,"E34.right")])],"isStart":true}),makeQuery(id+"F3.opExtrude","CAP_FACE",FACE,{"disambiguationData":[OSD([sQuery(id+"F2.wireOp",EDGE,"E35.bottom"),sQuery(id+"F2.wireOp",EDGE,"E35.top"),sQuery(id+"F2.wireOp",EDGE,"E35.left"),sQuery(id+"F2.wireOp",EDGE,"E35.right")])],"isStart":true})]});
            var sketch = newSketch(context, id + "F10", { "sketchPlane" : qUnion([Q0])});
            skLineSegment(sketch, "E44.bottom", {"start": v(-22.99, -76.2) * mm, "end": v(22.99, -76.2) * mm});
            skLineSegment(sketch, "E44.top", {"start": v(-22.99, -88.9) * mm, "end": v(22.99, -88.9) * mm});
            skLineSegment(sketch, "E44.left", {"start": v(-22.99, -76.2) * mm, "end": v(-22.99, -88.9) * mm});
            skLineSegment(sketch, "E44.right", {"start": v(22.99, -76.2) * mm, "end": v(22.99, -88.9) * mm});
            skPoint(sketch, "E45.firstSnap0", {"position": v(-22.99, 0) * mm});
            skLineSegment(sketch, "E45.bottom", {"start": v(-22.99, 76.2) * mm, "end": v(22.99, 76.2) * mm});
            skLineSegment(sketch, "E45.top", {"start": v(-22.99, 88.9) * mm, "end": v(22.99, 88.9) * mm});
            skLineSegment(sketch, "E45.left", {"start": v(-22.99, 76.2) * mm, "end": v(-22.99, 88.9) * mm});
            skLineSegment(sketch, "E45.right", {"start": v(22.99, 76.2) * mm, "end": v(22.99, 88.9) * mm});
            skSolve(sketch);
        }
        {
            var Q0;
            Q0 = qSketchRegion(id + "F10", true);
            extrude(context, id + "F11", {"entities" : qUnion([Q0]), "operationType" : NewBodyOperationType.ADD, "oppositeDirection" : true, "depth" : 1.02 * mm});
        }
        {
            var Q0;
            Q0=makeQuery(id+"F1.opExtrude","CAP_FACE",FACE,{"disambiguationData":[OSD([sQuery(id+"F0.wireOp",EDGE,"E0"),sQuery(id+"F0.wireOp",EDGE,"E1"),sQuery(id+"F0.wireOp",EDGE,"E2"),sQuery(id+"F0.wireOp",EDGE,"E3"),sQuery(id+"F0.wireOp",EDGE,"E7"),sQuery(id+"F0.wireOp",EDGE,"E8"),sQuery(id+"F0.wireOp",EDGE,"E9"),sQuery(id+"F0.wireOp",EDGE,"E10"),sQuery(id+"F0.wireOp",EDGE,"E11"),sQuery(id+"F0.wireOp",EDGE,"E12"),sQuery(id+"F0.wireOp",EDGE,"E14"),sQuery(id+"F0.wireOp",EDGE,"E15"),sQuery(id+"F0.wireOp",EDGE,"E19.bottom"),sQuery(id+"F0.wireOp",EDGE,"E19.top"),sQuery(id+"F0.wireOp",EDGE,"E19.left"),sQuery(id+"F0.wireOp",EDGE,"E19.right"),sQuery(id+"F0.wireOp",EDGE,"E22"),sQuery(id+"F0.wireOp",EDGE,"E23"),sQuery(id+"F0.wireOp",EDGE,"E24"),sQuery(id+"F0.wireOp",EDGE,"E25"),sQuery(id+"F0.wireOp",EDGE,"E29"),sQuery(id+"F0.wireOp",EDGE,"E30"),sQuery(id+"F0.wireOp",EDGE,"E31"),sQuery(id+"F0.wireOp",EDGE,"E32")])],"isStart":false});
            var sketch = newSketch(context, id + "F12", { "sketchPlane" : qUnion([Q0])});
            skLineSegment(sketch, "E46.bottom", {"start": v(-22.99, 76.2) * mm, "end": v(22.99, 76.2) * mm});
            skLineSegment(sketch, "E46.top", {"start": v(-22.99, -76.2) * mm, "end": v(22.99, -76.2) * mm});
            skLineSegment(sketch, "E46.left", {"start": v(-22.99, 76.2) * mm, "end": v(-22.99, -76.2) * mm});
            skLineSegment(sketch, "E46.right", {"start": v(22.99, 76.2) * mm, "end": v(22.99, -76.2) * mm});
            skArc(sketch, "E47", {"start": v(-10.17, 48.09) * mm, "mid": v(-17.7, 40.6) * mm, "end": v(-20.45, 30.35) * mm});
            skArc(sketch, "E48", {"start": v(-10.17, 48.09) * mm, "mid": v(-8.3, 49.95) * mm, "end": v(-7.62, 52.5) * mm});
            skArc(sketch, "E49", {"start": v(-2.54, 73.66) * mm, "mid": v(-6.13, 72.17) * mm, "end": v(-7.62, 68.58) * mm});
            skArc(sketch, "E50", {"start": v(7.62, 68.58) * mm, "mid": v(6.13, 72.17) * mm, "end": v(2.54, 73.66) * mm});
            skArc(sketch, "E51", {"start": v(7.62, 52.5) * mm, "mid": v(8.3, 49.95) * mm, "end": v(10.17, 48.09) * mm});
            skArc(sketch, "E52", {"start": v(20.45, 30.35) * mm, "mid": v(17.7, 40.6) * mm, "end": v(10.17, 48.09) * mm});
            skArc(sketch, "E53", {"start": v(-20.45, -30.35) * mm, "mid": v(-17.7, -40.6) * mm, "end": v(-10.17, -48.09) * mm});
            skArc(sketch, "E54", {"start": v(10.17, -48.09) * mm, "mid": v(17.7, -40.6) * mm, "end": v(20.45, -30.35) * mm});
            skArc(sketch, "E55", {"start": v(10.17, -48.09) * mm, "mid": v(8.3, -49.95) * mm, "end": v(7.62, -52.5) * mm});
            skArc(sketch, "E56", {"start": v(-7.62, -52.5) * mm, "mid": v(-8.3, -49.95) * mm, "end": v(-10.17, -48.09) * mm});
            skArc(sketch, "E57", {"start": v(-7.62, -68.58) * mm, "mid": v(-6.13, -72.17) * mm, "end": v(-2.54, -73.66) * mm});
            skArc(sketch, "E58", {"start": v(2.54, -73.66) * mm, "mid": v(6.13, -72.17) * mm, "end": v(7.62, -68.58) * mm});
            skLineSegment(sketch, "E59", {"start": v(-2.54, 73.66) * mm, "end": v(2.54, 73.66) * mm});
            skLineSegment(sketch, "E60", {"start": v(7.62, 68.58) * mm, "end": v(7.62, 52.5) * mm});
            skLineSegment(sketch, "E61", {"start": v(-7.62, 52.5) * mm, "end": v(-7.62, 68.58) * mm});
            skLineSegment(sketch, "E62", {"start": v(-20.45, 30.35) * mm, "end": v(-20.45, -30.35) * mm});
            skLineSegment(sketch, "E63", {"start": v(20.45, -30.35) * mm, "end": v(20.45, 30.35) * mm});
            skLineSegment(sketch, "E64", {"start": v(-7.62, -52.5) * mm, "end": v(-7.62, -68.58) * mm});
            skLineSegment(sketch, "E65", {"start": v(-2.54, -73.66) * mm, "end": v(2.54, -73.66) * mm});
            skLineSegment(sketch, "E66", {"start": v(7.62, -68.58) * mm, "end": v(7.62, -52.5) * mm});
            skCircle(sketch, "E67", {"center": v(-19.3, 45.09) * mm, "radius": 1.9 * mm});
            skCircle(sketch, "E68", {"center": v(19.3, 45.09) * mm, "radius": 1.9 * mm});
            skCircle(sketch, "E69", {"center": v(-19.3, -45.09) * mm, "radius": 1.9 * mm});
            skCircle(sketch, "E70", {"center": v(19.3, -45.09) * mm, "radius": 1.9 * mm});
            skSolve(sketch);
        }
        {
            var Q0;
            Q0 = qSketchRegion(id + "F12", true);
            extrude(context, id + "F13", {"entities" : qUnion([Q0]), "depth" : 6.35 * mm});
        }
        {
            var Q0;
            Q0=makeQuery(id+"F13.opExtrude","CAP_FACE",FACE,{"disambiguationData":[OSD([sQuery(id+"F12.wireOp",EDGE,"E46.bottom"),sQuery(id+"F12.wireOp",EDGE,"E46.top"),sQuery(id+"F12.wireOp",EDGE,"E46.left"),sQuery(id+"F12.wireOp",EDGE,"E46.right"),sQuery(id+"F12.wireOp",EDGE,"E47"),sQuery(id+"F12.wireOp",EDGE,"E48"),sQuery(id+"F12.wireOp",EDGE,"E49"),sQuery(id+"F12.wireOp",EDGE,"E50"),sQuery(id+"F12.wireOp",EDGE,"E51"),sQuery(id+"F12.wireOp",EDGE,"E52"),sQuery(id+"F12.wireOp",EDGE,"E53"),sQuery(id+"F12.wireOp",EDGE,"E54"),sQuery(id+"F12.wireOp",EDGE,"E55"),sQuery(id+"F12.wireOp",EDGE,"E56"),sQuery(id+"F12.wireOp",EDGE,"E57"),sQuery(id+"F12.wireOp",EDGE,"E58"),sQuery(id+"F12.wireOp",EDGE,"E59"),sQuery(id+"F12.wireOp",EDGE,"E60"),sQuery(id+"F12.wireOp",EDGE,"E61"),sQuery(id+"F12.wireOp",EDGE,"E62"),sQuery(id+"F12.wireOp",EDGE,"E63"),sQuery(id+"F12.wireOp",EDGE,"E64"),sQuery(id+"F12.wireOp",EDGE,"E65"),sQuery(id+"F12.wireOp",EDGE,"E66"),sQuery(id+"F12.wireOp",EDGE,"E67"),sQuery(id+"F12.wireOp",EDGE,"E68"),sQuery(id+"F12.wireOp",EDGE,"E69"),sQuery(id+"F12.wireOp",EDGE,"E70")])],"isStart":false});
            var sketch = newSketch(context, id + "F14", { "sketchPlane" : qUnion([Q0])});
            skLineSegment(sketch, "E71.bottom", {"start": v(-22.99, 76.2) * mm, "end": v(22.99, 76.2) * mm});
            skLineSegment(sketch, "E71.top", {"start": v(-22.99, -76.2) * mm, "end": v(22.99, -76.2) * mm});
            skLineSegment(sketch, "E71.left", {"start": v(-22.99, 76.2) * mm, "end": v(-22.99, -76.2) * mm});
            skLineSegment(sketch, "E71.right", {"start": v(22.99, 76.2) * mm, "end": v(22.99, -76.2) * mm});
            skCircle(sketch, "E72", {"center": v(19.3, 45.09) * mm, "radius": 1.9 * mm});
            skCircle(sketch, "E73", {"center": v(-19.3, 45.09) * mm, "radius": 1.9 * mm});
            skCircle(sketch, "E74", {"center": v(-19.3, -45.09) * mm, "radius": 1.9 * mm});
            skCircle(sketch, "E75", {"center": v(19.3, -45.09) * mm, "radius": 1.9 * mm});
            skSolve(sketch);
        }
        {
            var Q0;
            Q0 = qSketchRegion(id + "F14", true);
            extrude(context, id + "F15", {"entities" : qUnion([Q0]), "operationType" : NewBodyOperationType.ADD, "depth" : 2.03 * mm});
        }
        {
            var Q0;
            Q0=makeQuery(id+"F15.opExtrude","CAP_FACE",FACE,{"disambiguationData":[OSD([sQuery(id+"F14.wireOp",EDGE,"E71.bottom"),sQuery(id+"F14.wireOp",EDGE,"E71.top"),sQuery(id+"F14.wireOp",EDGE,"E71.left"),sQuery(id+"F14.wireOp",EDGE,"E71.right"),sQuery(id+"F14.wireOp",EDGE,"E72"),sQuery(id+"F14.wireOp",EDGE,"E73"),sQuery(id+"F14.wireOp",EDGE,"E74"),sQuery(id+"F14.wireOp",EDGE,"E75")])],"isStart":false});
            var sketch = newSketch(context, id + "F16", { "sketchPlane" : qUnion([Q0])});
            skLineSegment(sketch, "E76.bottom", {"start": v(-14.86, 39.37) * mm, "end": v(14.86, 39.37) * mm});
            skLineSegment(sketch, "E76.top", {"start": v(-14.86, -20.32) * mm, "end": v(14.86, -20.32) * mm});
            skLineSegment(sketch, "E76.left", {"start": v(-14.86, 39.37) * mm, "end": v(-14.86, -20.32) * mm});
            skLineSegment(sketch, "E76.right", {"start": v(14.86, 39.37) * mm, "end": v(14.86, -20.32) * mm});
            skPoint(sketch, "E77", {"position": v(0, 76.2) * mm});
            skPoint(sketch, "E78", {"position": v(0, 39.37) * mm});
            skSolve(sketch);
        }
        {
            var Q0;
            Q0 = qSketchRegion(id + "F16", true);
            var Q1;
            Q1=makeQuery(id+"F15.opExtrude","CAP_FACE",FACE,{"disambiguationData":[OSD([sQuery(id+"F14.wireOp",EDGE,"E71.bottom"),sQuery(id+"F14.wireOp",EDGE,"E71.top"),sQuery(id+"F14.wireOp",EDGE,"E71.left"),sQuery(id+"F14.wireOp",EDGE,"E71.right"),sQuery(id+"F14.wireOp",EDGE,"E72"),sQuery(id+"F14.wireOp",EDGE,"E73"),sQuery(id+"F14.wireOp",EDGE,"E74"),sQuery(id+"F14.wireOp",EDGE,"E75")])],"isStart":true});
            extrude(context, id + "F17", {"entities" : qUnion([Q0]), "operationType" : NewBodyOperationType.REMOVE, "endBound" : BoundingType.UP_TO_SURFACE, "oppositeDirection" : true, "endBoundEntityFace" : qUnion([Q1]), "depth" : 25.4 * mm});
        }
        {
            var Q0;
            Q0=makeQuery(id+"F15.boolean.opBoolean","MERGE",EDGE,{"derivedFrom":[makeQuery(id+"F13.opExtrude","SWEPT_EDGE",EDGE,{"disambiguationData":[OSD([sQuery(id+"F12.wireOp",EDGE,"E46.bottom"),sQuery(id+"F12.wireOp",EDGE,"E46.left")])]}),makeQuery(id+"F15.opExtrude","SWEPT_EDGE",EDGE,{"disambiguationData":[OSD([sQuery(id+"F14.wireOp",EDGE,"E71.bottom"),sQuery(id+"F14.wireOp",EDGE,"E71.left")])]})]});
            var Q1;
            Q1=makeQuery(id+"F15.boolean.opBoolean","MERGE",EDGE,{"derivedFrom":[makeQuery(id+"F13.opExtrude","SWEPT_EDGE",EDGE,{"disambiguationData":[OSD([sQuery(id+"F12.wireOp",EDGE,"E46.bottom"),sQuery(id+"F12.wireOp",EDGE,"E46.right")])]}),makeQuery(id+"F15.opExtrude","SWEPT_EDGE",EDGE,{"disambiguationData":[OSD([sQuery(id+"F14.wireOp",EDGE,"E71.bottom"),sQuery(id+"F14.wireOp",EDGE,"E71.right")])]})]});
            var Q2;
            Q2=makeQuery(id+"F15.boolean.opBoolean","MERGE",EDGE,{"derivedFrom":[makeQuery(id+"F13.opExtrude","SWEPT_EDGE",EDGE,{"disambiguationData":[OSD([sQuery(id+"F12.wireOp",EDGE,"E46.top"),sQuery(id+"F12.wireOp",EDGE,"E46.right")])]}),makeQuery(id+"F15.opExtrude","SWEPT_EDGE",EDGE,{"disambiguationData":[OSD([sQuery(id+"F14.wireOp",EDGE,"E71.top"),sQuery(id+"F14.wireOp",EDGE,"E71.right")])]})]});
            var Q3;
            Q3=makeQuery(id+"F15.boolean.opBoolean","MERGE",EDGE,{"derivedFrom":[makeQuery(id+"F13.opExtrude","SWEPT_EDGE",EDGE,{"disambiguationData":[OSD([sQuery(id+"F12.wireOp",EDGE,"E46.top"),sQuery(id+"F12.wireOp",EDGE,"E46.left")])]}),makeQuery(id+"F15.opExtrude","SWEPT_EDGE",EDGE,{"disambiguationData":[OSD([sQuery(id+"F14.wireOp",EDGE,"E71.top"),sQuery(id+"F14.wireOp",EDGE,"E71.left")])]})]});
            var Q4;
            Q4=makeQuery(id+"F17.boolean.opBoolean","COPY",EDGE,{"derivedFrom":makeQuery(id+"F17.opExtrude","SWEPT_EDGE",EDGE,{"disambiguationData":[OSD([sQuery(id+"F16.wireOp",EDGE,"E76.bottom"),sQuery(id+"F16.wireOp",EDGE,"E76.left")])]})});
            var Q5;
            Q5=makeQuery(id+"F17.boolean.opBoolean","COPY",EDGE,{"derivedFrom":makeQuery(id+"F17.opExtrude","SWEPT_EDGE",EDGE,{"disambiguationData":[OSD([sQuery(id+"F16.wireOp",EDGE,"E76.bottom"),sQuery(id+"F16.wireOp",EDGE,"E76.right")])]})});
            var Q6;
            Q6=makeQuery(id+"F17.boolean.opBoolean","COPY",EDGE,{"derivedFrom":makeQuery(id+"F17.opExtrude","SWEPT_EDGE",EDGE,{"disambiguationData":[OSD([sQuery(id+"F16.wireOp",EDGE,"E76.top"),sQuery(id+"F16.wireOp",EDGE,"E76.left")])]})});
            var Q7;
            Q7=makeQuery(id+"F17.boolean.opBoolean","COPY",EDGE,{"derivedFrom":makeQuery(id+"F17.opExtrude","SWEPT_EDGE",EDGE,{"disambiguationData":[OSD([sQuery(id+"F16.wireOp",EDGE,"E76.top"),sQuery(id+"F16.wireOp",EDGE,"E76.right")])]})});
            fillet(context, id + "F18", {"entities" : qUnion([Q0, Q1, Q2, Q3, Q4, Q5, Q6, Q7]), "radius" : 5.08 * mm, "tangentPropagation" : true, "allowEdgeOverflow" : false});
        }
        {
            var Q0;
            Q0=makeQuery(id+"F13.opExtrude","CAP_FACE",FACE,{"disambiguationData":[OSD([sQuery(id+"F12.wireOp",EDGE,"E46.bottom"),sQuery(id+"F12.wireOp",EDGE,"E46.top"),sQuery(id+"F12.wireOp",EDGE,"E46.left"),sQuery(id+"F12.wireOp",EDGE,"E46.right"),sQuery(id+"F12.wireOp",EDGE,"E47"),sQuery(id+"F12.wireOp",EDGE,"E48"),sQuery(id+"F12.wireOp",EDGE,"E49"),sQuery(id+"F12.wireOp",EDGE,"E50"),sQuery(id+"F12.wireOp",EDGE,"E51"),sQuery(id+"F12.wireOp",EDGE,"E52"),sQuery(id+"F12.wireOp",EDGE,"E53"),sQuery(id+"F12.wireOp",EDGE,"E54"),sQuery(id+"F12.wireOp",EDGE,"E55"),sQuery(id+"F12.wireOp",EDGE,"E56"),sQuery(id+"F12.wireOp",EDGE,"E57"),sQuery(id+"F12.wireOp",EDGE,"E58"),sQuery(id+"F12.wireOp",EDGE,"E59"),sQuery(id+"F12.wireOp",EDGE,"E60"),sQuery(id+"F12.wireOp",EDGE,"E61"),sQuery(id+"F12.wireOp",EDGE,"E62"),sQuery(id+"F12.wireOp",EDGE,"E63"),sQuery(id+"F12.wireOp",EDGE,"E64"),sQuery(id+"F12.wireOp",EDGE,"E65"),sQuery(id+"F12.wireOp",EDGE,"E66"),sQuery(id+"F12.wireOp",EDGE,"E67"),sQuery(id+"F12.wireOp",EDGE,"E68"),sQuery(id+"F12.wireOp",EDGE,"E69"),sQuery(id+"F12.wireOp",EDGE,"E70")])],"isStart":true});
            shell(context, id + "F19", {"entities" : qUnion([Q0]), "thickness" : 2.54 * mm});
        }
        {
            var Q0;
            Q0=makeQuery(id+"F19.opShell","TWEAK_EDGE",EDGE,{"derivedFrom":[makeQuery(id+"F15.boolean.opBoolean","MERGE",FACE,{"derivedFrom":[makeQuery(id+"F13.opExtrude","SWEPT_FACE",FACE,{"disambiguationData":[OSD([sQuery(id+"F12.wireOp",EDGE,"E70")])]}),makeQuery(id+"F15.opExtrude","SWEPT_FACE",FACE,{"disambiguationData":[OSD([sQuery(id+"F14.wireOp",EDGE,"E75")])]})]}),makeQuery(id+"F15.boolean.opBoolean","MERGE",FACE,{"derivedFrom":[makeQuery(id+"F13.opExtrude","SWEPT_FACE",FACE,{"disambiguationData":[OSD([sQuery(id+"F12.wireOp",EDGE,"E46.right")])]}),makeQuery(id+"F15.opExtrude","SWEPT_FACE",FACE,{"disambiguationData":[OSD([sQuery(id+"F14.wireOp",EDGE,"E71.right")])]})]})]});
            var Q1;
            Q1=makeQuery(id+"F19.opShell","TWEAK_EDGE",EDGE,{"derivedFrom":[makeQuery(id+"F13.opExtrude","SWEPT_FACE",FACE,{"disambiguationData":[OSD([sQuery(id+"F12.wireOp",EDGE,"E54")])]}),makeQuery(id+"F15.boolean.opBoolean","MERGE",FACE,{"derivedFrom":[makeQuery(id+"F13.opExtrude","SWEPT_FACE",FACE,{"disambiguationData":[OSD([sQuery(id+"F12.wireOp",EDGE,"E70")])]}),makeQuery(id+"F15.opExtrude","SWEPT_FACE",FACE,{"disambiguationData":[OSD([sQuery(id+"F14.wireOp",EDGE,"E75")])]})]})]});
            var Q2;
            Q2=makeQuery(id+"F19.opShell","TWEAK_EDGE",EDGE,{"derivedFrom":[makeQuery(id+"F13.opExtrude","SWEPT_FACE",FACE,{"disambiguationData":[OSD([sQuery(id+"F12.wireOp",EDGE,"E53")])]}),makeQuery(id+"F15.boolean.opBoolean","MERGE",FACE,{"derivedFrom":[makeQuery(id+"F13.opExtrude","SWEPT_FACE",FACE,{"disambiguationData":[OSD([sQuery(id+"F12.wireOp",EDGE,"E69")])]}),makeQuery(id+"F15.opExtrude","SWEPT_FACE",FACE,{"disambiguationData":[OSD([sQuery(id+"F14.wireOp",EDGE,"E74")])]})]})]});
            var Q3;
            Q3=makeQuery(id+"F19.opShell","TWEAK_EDGE",EDGE,{"derivedFrom":[makeQuery(id+"F13.opExtrude","SWEPT_FACE",FACE,{"disambiguationData":[OSD([sQuery(id+"F12.wireOp",EDGE,"E57")])]}),makeQuery(id+"F15.boolean.opBoolean","MERGE",FACE,{"derivedFrom":[makeQuery(id+"F13.opExtrude","SWEPT_FACE",FACE,{"disambiguationData":[OSD([sQuery(id+"F12.wireOp",EDGE,"E46.top")])]}),makeQuery(id+"F15.opExtrude","SWEPT_FACE",FACE,{"disambiguationData":[OSD([sQuery(id+"F14.wireOp",EDGE,"E71.top")])]})]})]});
            var Q4;
            Q4=makeQuery(id+"F19.opShell","TWEAK_EDGE",EDGE,{"derivedFrom":[makeQuery(id+"F15.boolean.opBoolean","MERGE",FACE,{"derivedFrom":[makeQuery(id+"F13.opExtrude","SWEPT_FACE",FACE,{"disambiguationData":[OSD([sQuery(id+"F12.wireOp",EDGE,"E69")])]}),makeQuery(id+"F15.opExtrude","SWEPT_FACE",FACE,{"disambiguationData":[OSD([sQuery(id+"F14.wireOp",EDGE,"E74")])]})]}),makeQuery(id+"F15.boolean.opBoolean","MERGE",FACE,{"derivedFrom":[makeQuery(id+"F13.opExtrude","SWEPT_FACE",FACE,{"disambiguationData":[OSD([sQuery(id+"F12.wireOp",EDGE,"E46.left")])]}),makeQuery(id+"F15.opExtrude","SWEPT_FACE",FACE,{"disambiguationData":[OSD([sQuery(id+"F14.wireOp",EDGE,"E71.left")])]})]})]});
            var Q5;
            Q5=makeQuery(id+"F19.opShell","TWEAK_EDGE",EDGE,{"derivedFrom":[makeQuery(id+"F13.opExtrude","SWEPT_FACE",FACE,{"disambiguationData":[OSD([sQuery(id+"F12.wireOp",EDGE,"E58")])]}),makeQuery(id+"F15.boolean.opBoolean","MERGE",FACE,{"derivedFrom":[makeQuery(id+"F13.opExtrude","SWEPT_FACE",FACE,{"disambiguationData":[OSD([sQuery(id+"F12.wireOp",EDGE,"E46.top")])]}),makeQuery(id+"F15.opExtrude","SWEPT_FACE",FACE,{"disambiguationData":[OSD([sQuery(id+"F14.wireOp",EDGE,"E71.top")])]})]})]});
            var Q6;
            Q6=makeQuery(id+"F19.opShell","TWEAK_EDGE",EDGE,{"derivedFrom":[makeQuery(id+"F15.boolean.opBoolean","MERGE",FACE,{"derivedFrom":[makeQuery(id+"F13.opExtrude","SWEPT_FACE",FACE,{"disambiguationData":[OSD([sQuery(id+"F12.wireOp",EDGE,"E67")])]}),makeQuery(id+"F15.opExtrude","SWEPT_FACE",FACE,{"disambiguationData":[OSD([sQuery(id+"F14.wireOp",EDGE,"E73")])]})]}),makeQuery(id+"F15.boolean.opBoolean","MERGE",FACE,{"derivedFrom":[makeQuery(id+"F13.opExtrude","SWEPT_FACE",FACE,{"disambiguationData":[OSD([sQuery(id+"F12.wireOp",EDGE,"E46.left")])]}),makeQuery(id+"F15.opExtrude","SWEPT_FACE",FACE,{"disambiguationData":[OSD([sQuery(id+"F14.wireOp",EDGE,"E71.left")])]})]})]});
            var Q7;
            Q7=makeQuery(id+"F19.opShell","TWEAK_EDGE",EDGE,{"derivedFrom":[makeQuery(id+"F13.opExtrude","SWEPT_FACE",FACE,{"disambiguationData":[OSD([sQuery(id+"F12.wireOp",EDGE,"E47")])]}),makeQuery(id+"F15.boolean.opBoolean","MERGE",FACE,{"derivedFrom":[makeQuery(id+"F13.opExtrude","SWEPT_FACE",FACE,{"disambiguationData":[OSD([sQuery(id+"F12.wireOp",EDGE,"E67")])]}),makeQuery(id+"F15.opExtrude","SWEPT_FACE",FACE,{"disambiguationData":[OSD([sQuery(id+"F14.wireOp",EDGE,"E73")])]})]})]});
            var Q8;
            Q8=makeQuery(id+"F19.opShell","TWEAK_EDGE",EDGE,{"derivedFrom":[makeQuery(id+"F13.opExtrude","SWEPT_FACE",FACE,{"disambiguationData":[OSD([sQuery(id+"F12.wireOp",EDGE,"E49")])]}),makeQuery(id+"F15.boolean.opBoolean","MERGE",FACE,{"derivedFrom":[makeQuery(id+"F13.opExtrude","SWEPT_FACE",FACE,{"disambiguationData":[OSD([sQuery(id+"F12.wireOp",EDGE,"E46.bottom")])]}),makeQuery(id+"F15.opExtrude","SWEPT_FACE",FACE,{"disambiguationData":[OSD([sQuery(id+"F14.wireOp",EDGE,"E71.bottom")])]})]})]});
            var Q9;
            Q9=makeQuery(id+"F19.opShell","TWEAK_EDGE",EDGE,{"derivedFrom":[makeQuery(id+"F13.opExtrude","SWEPT_FACE",FACE,{"disambiguationData":[OSD([sQuery(id+"F12.wireOp",EDGE,"E50")])]}),makeQuery(id+"F15.boolean.opBoolean","MERGE",FACE,{"derivedFrom":[makeQuery(id+"F13.opExtrude","SWEPT_FACE",FACE,{"disambiguationData":[OSD([sQuery(id+"F12.wireOp",EDGE,"E46.bottom")])]}),makeQuery(id+"F15.opExtrude","SWEPT_FACE",FACE,{"disambiguationData":[OSD([sQuery(id+"F14.wireOp",EDGE,"E71.bottom")])]})]})]});
            var Q10;
            Q10=makeQuery(id+"F19.opShell","TWEAK_EDGE",EDGE,{"derivedFrom":[makeQuery(id+"F15.boolean.opBoolean","MERGE",FACE,{"derivedFrom":[makeQuery(id+"F13.opExtrude","SWEPT_FACE",FACE,{"disambiguationData":[OSD([sQuery(id+"F12.wireOp",EDGE,"E68")])]}),makeQuery(id+"F15.opExtrude","SWEPT_FACE",FACE,{"disambiguationData":[OSD([sQuery(id+"F14.wireOp",EDGE,"E72")])]})]}),makeQuery(id+"F15.boolean.opBoolean","MERGE",FACE,{"derivedFrom":[makeQuery(id+"F13.opExtrude","SWEPT_FACE",FACE,{"disambiguationData":[OSD([sQuery(id+"F12.wireOp",EDGE,"E46.right")])]}),makeQuery(id+"F15.opExtrude","SWEPT_FACE",FACE,{"disambiguationData":[OSD([sQuery(id+"F14.wireOp",EDGE,"E71.right")])]})]})]});
            var Q11;
            Q11=makeQuery(id+"F19.opShell","TWEAK_EDGE",EDGE,{"derivedFrom":[makeQuery(id+"F13.opExtrude","SWEPT_FACE",FACE,{"disambiguationData":[OSD([sQuery(id+"F12.wireOp",EDGE,"E52")])]}),makeQuery(id+"F15.boolean.opBoolean","MERGE",FACE,{"derivedFrom":[makeQuery(id+"F13.opExtrude","SWEPT_FACE",FACE,{"disambiguationData":[OSD([sQuery(id+"F12.wireOp",EDGE,"E68")])]}),makeQuery(id+"F15.opExtrude","SWEPT_FACE",FACE,{"disambiguationData":[OSD([sQuery(id+"F14.wireOp",EDGE,"E72")])]})]})]});
            fillet(context, id + "F20", {"entities" : qUnion([Q0, Q1, Q2, Q3, Q4, Q5, Q6, Q7, Q8, Q9, Q10, Q11]), "radius" : 1.27 * mm, "tangentPropagation" : true, "allowEdgeOverflow" : false});
        }
    });
